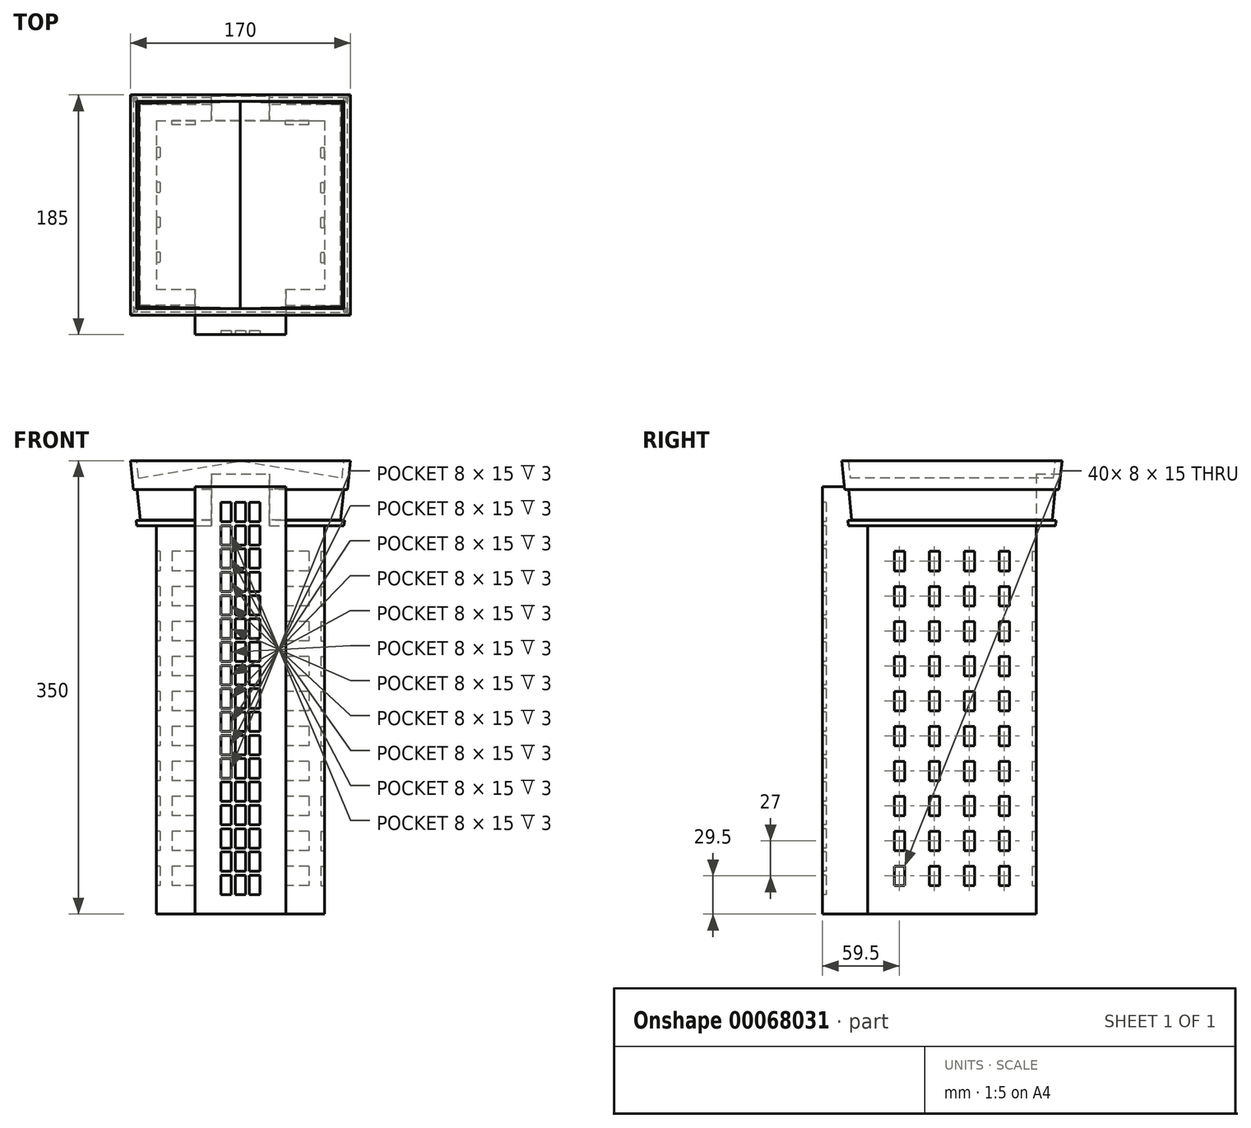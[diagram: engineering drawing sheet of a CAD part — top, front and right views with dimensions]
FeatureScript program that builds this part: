
annotation { "Feature Type Name" : "Feature", "Feature Type Description" : "" }
export const myFeature = defineFeature(function(context is Context, id is Id, definition is map)
    precondition{}
    {
        {
            var Q0;
            Q0=qCreatedBy(makeId("Top.planeOp"),FACE);
            var sketch = newSketch(context, id + "F0", { "sketchPlane" : qUnion([Q0])});
            skLineSegment(sketch, "E0.bottom", {"start": v(0, 0) * mm, "end": v(130, 0) * mm});
            skLineSegment(sketch, "E0.top", {"start": v(0, -130) * mm, "end": v(130, -130) * mm});
            skLineSegment(sketch, "E0.left", {"start": v(0, 0) * mm, "end": v(0, -130) * mm});
            skLineSegment(sketch, "E0.right", {"start": v(130, 0) * mm, "end": v(130, -130) * mm});
            skSolve(sketch);
        }
        {
            var Q0;
            Q0 = qSketchRegion(id + "F0", true);
            extrude(context, id + "F1", {"entities" : qUnion([Q0]), "depth" : 300 * mm});
        }
        {
            var Q0;
            Q0=makeQuery(id+"F1.opExtrude","SWEPT_FACE",FACE,{"disambiguationData":[OSD([sQuery(id+"F0.wireOp",EDGE,"E0.right")])]});
            var sketch = newSketch(context, id + "F2", { "sketchPlane" : qUnion([Q0])});
            skLineSegment(sketch, "E1.bottom", {"start": v(-109.5, 280) * mm, "end": v(-101.5, 280) * mm});
            skLineSegment(sketch, "E1.top", {"start": v(-109.5, 265) * mm, "end": v(-101.5, 265) * mm});
            skLineSegment(sketch, "E1.left", {"start": v(-109.5, 280) * mm, "end": v(-109.5, 265) * mm});
            skLineSegment(sketch, "E1.right", {"start": v(-101.5, 280) * mm, "end": v(-101.5, 265) * mm});
            skLineSegment(sketch, "E2.0.1.0", {"start": v(-109.5, 253) * mm, "end": v(-101.5, 253) * mm});
            skLineSegment(sketch, "E2.0.1.1", {"start": v(-109.5, 238) * mm, "end": v(-101.5, 238) * mm});
            skLineSegment(sketch, "E2.0.1.2", {"start": v(-109.5, 253) * mm, "end": v(-109.5, 238) * mm});
            skLineSegment(sketch, "E2.0.1.3", {"start": v(-101.5, 253) * mm, "end": v(-101.5, 238) * mm});
            skLineSegment(sketch, "E2.0.2.0", {"start": v(-109.5, 226) * mm, "end": v(-101.5, 226) * mm});
            skLineSegment(sketch, "E2.0.2.1", {"start": v(-109.5, 211) * mm, "end": v(-101.5, 211) * mm});
            skLineSegment(sketch, "E2.0.2.2", {"start": v(-109.5, 226) * mm, "end": v(-109.5, 211) * mm});
            skLineSegment(sketch, "E2.0.2.3", {"start": v(-101.5, 226) * mm, "end": v(-101.5, 211) * mm});
            skLineSegment(sketch, "E2.0.3.0", {"start": v(-109.5, 199) * mm, "end": v(-101.5, 199) * mm});
            skLineSegment(sketch, "E2.0.3.1", {"start": v(-109.5, 184) * mm, "end": v(-101.5, 184) * mm});
            skLineSegment(sketch, "E2.0.3.2", {"start": v(-109.5, 199) * mm, "end": v(-109.5, 184) * mm});
            skLineSegment(sketch, "E2.0.3.3", {"start": v(-101.5, 199) * mm, "end": v(-101.5, 184) * mm});
            skLineSegment(sketch, "E2.0.4.0", {"start": v(-109.5, 172) * mm, "end": v(-101.5, 172) * mm});
            skLineSegment(sketch, "E2.0.4.1", {"start": v(-109.5, 157) * mm, "end": v(-101.5, 157) * mm});
            skLineSegment(sketch, "E2.0.4.2", {"start": v(-109.5, 172) * mm, "end": v(-109.5, 157) * mm});
            skLineSegment(sketch, "E2.0.4.3", {"start": v(-101.5, 172) * mm, "end": v(-101.5, 157) * mm});
            skLineSegment(sketch, "E2.0.5.0", {"start": v(-109.5, 145) * mm, "end": v(-101.5, 145) * mm});
            skLineSegment(sketch, "E2.0.5.1", {"start": v(-109.5, 130) * mm, "end": v(-101.5, 130) * mm});
            skLineSegment(sketch, "E2.0.5.2", {"start": v(-109.5, 145) * mm, "end": v(-109.5, 130) * mm});
            skLineSegment(sketch, "E2.0.5.3", {"start": v(-101.5, 145) * mm, "end": v(-101.5, 130) * mm});
            skLineSegment(sketch, "E2.0.6.0", {"start": v(-109.5, 118) * mm, "end": v(-101.5, 118) * mm});
            skLineSegment(sketch, "E2.0.6.1", {"start": v(-109.5, 103) * mm, "end": v(-101.5, 103) * mm});
            skLineSegment(sketch, "E2.0.6.2", {"start": v(-109.5, 118) * mm, "end": v(-109.5, 103) * mm});
            skLineSegment(sketch, "E2.0.6.3", {"start": v(-101.5, 118) * mm, "end": v(-101.5, 103) * mm});
            skLineSegment(sketch, "E2.0.7.0", {"start": v(-109.5, 91) * mm, "end": v(-101.5, 91) * mm});
            skLineSegment(sketch, "E2.0.7.1", {"start": v(-109.5, 76) * mm, "end": v(-101.5, 76) * mm});
            skLineSegment(sketch, "E2.0.7.2", {"start": v(-109.5, 91) * mm, "end": v(-109.5, 76) * mm});
            skLineSegment(sketch, "E2.0.7.3", {"start": v(-101.5, 91) * mm, "end": v(-101.5, 76) * mm});
            skLineSegment(sketch, "E2.0.8.0", {"start": v(-109.5, 64) * mm, "end": v(-101.5, 64) * mm});
            skLineSegment(sketch, "E2.0.8.1", {"start": v(-109.5, 49) * mm, "end": v(-101.5, 49) * mm});
            skLineSegment(sketch, "E2.0.8.2", {"start": v(-109.5, 64) * mm, "end": v(-109.5, 49) * mm});
            skLineSegment(sketch, "E2.0.8.3", {"start": v(-101.5, 64) * mm, "end": v(-101.5, 49) * mm});
            skLineSegment(sketch, "E2.0.9.0", {"start": v(-109.5, 37) * mm, "end": v(-101.5, 37) * mm});
            skLineSegment(sketch, "E2.0.9.1", {"start": v(-109.5, 22) * mm, "end": v(-101.5, 22) * mm});
            skLineSegment(sketch, "E2.0.9.2", {"start": v(-109.5, 37) * mm, "end": v(-109.5, 22) * mm});
            skLineSegment(sketch, "E2.0.9.3", {"start": v(-101.5, 37) * mm, "end": v(-101.5, 22) * mm});
            skLineSegment(sketch, "E2.1.0.0", {"start": v(-82.5, 280) * mm, "end": v(-74.5, 280) * mm});
            skLineSegment(sketch, "E2.1.0.1", {"start": v(-82.5, 265) * mm, "end": v(-74.5, 265) * mm});
            skLineSegment(sketch, "E2.1.0.2", {"start": v(-82.5, 280) * mm, "end": v(-82.5, 265) * mm});
            skLineSegment(sketch, "E2.1.0.3", {"start": v(-74.5, 280) * mm, "end": v(-74.5, 265) * mm});
            skLineSegment(sketch, "E2.1.1.0", {"start": v(-82.5, 253) * mm, "end": v(-74.5, 253) * mm});
            skLineSegment(sketch, "E2.1.1.1", {"start": v(-82.5, 238) * mm, "end": v(-74.5, 238) * mm});
            skLineSegment(sketch, "E2.1.1.2", {"start": v(-82.5, 253) * mm, "end": v(-82.5, 238) * mm});
            skLineSegment(sketch, "E2.1.1.3", {"start": v(-74.5, 253) * mm, "end": v(-74.5, 238) * mm});
            skLineSegment(sketch, "E2.1.2.0", {"start": v(-82.5, 226) * mm, "end": v(-74.5, 226) * mm});
            skLineSegment(sketch, "E2.1.2.1", {"start": v(-82.5, 211) * mm, "end": v(-74.5, 211) * mm});
            skLineSegment(sketch, "E2.1.2.2", {"start": v(-82.5, 226) * mm, "end": v(-82.5, 211) * mm});
            skLineSegment(sketch, "E2.1.2.3", {"start": v(-74.5, 226) * mm, "end": v(-74.5, 211) * mm});
            skLineSegment(sketch, "E2.1.3.0", {"start": v(-82.5, 199) * mm, "end": v(-74.5, 199) * mm});
            skLineSegment(sketch, "E2.1.3.1", {"start": v(-82.5, 184) * mm, "end": v(-74.5, 184) * mm});
            skLineSegment(sketch, "E2.1.3.2", {"start": v(-82.5, 199) * mm, "end": v(-82.5, 184) * mm});
            skLineSegment(sketch, "E2.1.3.3", {"start": v(-74.5, 199) * mm, "end": v(-74.5, 184) * mm});
            skLineSegment(sketch, "E2.1.4.0", {"start": v(-82.5, 172) * mm, "end": v(-74.5, 172) * mm});
            skLineSegment(sketch, "E2.1.4.1", {"start": v(-82.5, 157) * mm, "end": v(-74.5, 157) * mm});
            skLineSegment(sketch, "E2.1.4.2", {"start": v(-82.5, 172) * mm, "end": v(-82.5, 157) * mm});
            skLineSegment(sketch, "E2.1.4.3", {"start": v(-74.5, 172) * mm, "end": v(-74.5, 157) * mm});
            skLineSegment(sketch, "E2.1.5.0", {"start": v(-82.5, 145) * mm, "end": v(-74.5, 145) * mm});
            skLineSegment(sketch, "E2.1.5.1", {"start": v(-82.5, 130) * mm, "end": v(-74.5, 130) * mm});
            skLineSegment(sketch, "E2.1.5.2", {"start": v(-82.5, 145) * mm, "end": v(-82.5, 130) * mm});
            skLineSegment(sketch, "E2.1.5.3", {"start": v(-74.5, 145) * mm, "end": v(-74.5, 130) * mm});
            skLineSegment(sketch, "E2.1.6.0", {"start": v(-82.5, 118) * mm, "end": v(-74.5, 118) * mm});
            skLineSegment(sketch, "E2.1.6.1", {"start": v(-82.5, 103) * mm, "end": v(-74.5, 103) * mm});
            skLineSegment(sketch, "E2.1.6.2", {"start": v(-82.5, 118) * mm, "end": v(-82.5, 103) * mm});
            skLineSegment(sketch, "E2.1.6.3", {"start": v(-74.5, 118) * mm, "end": v(-74.5, 103) * mm});
            skLineSegment(sketch, "E2.1.7.0", {"start": v(-82.5, 91) * mm, "end": v(-74.5, 91) * mm});
            skLineSegment(sketch, "E2.1.7.1", {"start": v(-82.5, 76) * mm, "end": v(-74.5, 76) * mm});
            skLineSegment(sketch, "E2.1.7.2", {"start": v(-82.5, 91) * mm, "end": v(-82.5, 76) * mm});
            skLineSegment(sketch, "E2.1.7.3", {"start": v(-74.5, 91) * mm, "end": v(-74.5, 76) * mm});
            skLineSegment(sketch, "E2.1.8.0", {"start": v(-82.5, 64) * mm, "end": v(-74.5, 64) * mm});
            skLineSegment(sketch, "E2.1.8.1", {"start": v(-82.5, 49) * mm, "end": v(-74.5, 49) * mm});
            skLineSegment(sketch, "E2.1.8.2", {"start": v(-82.5, 64) * mm, "end": v(-82.5, 49) * mm});
            skLineSegment(sketch, "E2.1.8.3", {"start": v(-74.5, 64) * mm, "end": v(-74.5, 49) * mm});
            skLineSegment(sketch, "E2.1.9.0", {"start": v(-82.5, 37) * mm, "end": v(-74.5, 37) * mm});
            skLineSegment(sketch, "E2.1.9.1", {"start": v(-82.5, 22) * mm, "end": v(-74.5, 22) * mm});
            skLineSegment(sketch, "E2.1.9.2", {"start": v(-82.5, 37) * mm, "end": v(-82.5, 22) * mm});
            skLineSegment(sketch, "E2.1.9.3", {"start": v(-74.5, 37) * mm, "end": v(-74.5, 22) * mm});
            skLineSegment(sketch, "E2.2.0.0", {"start": v(-55.5, 280) * mm, "end": v(-47.5, 280) * mm});
            skLineSegment(sketch, "E2.2.0.1", {"start": v(-55.5, 265) * mm, "end": v(-47.5, 265) * mm});
            skLineSegment(sketch, "E2.2.0.2", {"start": v(-55.5, 280) * mm, "end": v(-55.5, 265) * mm});
            skLineSegment(sketch, "E2.2.0.3", {"start": v(-47.5, 280) * mm, "end": v(-47.5, 265) * mm});
            skLineSegment(sketch, "E2.2.1.0", {"start": v(-55.5, 253) * mm, "end": v(-47.5, 253) * mm});
            skLineSegment(sketch, "E2.2.1.1", {"start": v(-55.5, 238) * mm, "end": v(-47.5, 238) * mm});
            skLineSegment(sketch, "E2.2.1.2", {"start": v(-55.5, 253) * mm, "end": v(-55.5, 238) * mm});
            skLineSegment(sketch, "E2.2.1.3", {"start": v(-47.5, 253) * mm, "end": v(-47.5, 238) * mm});
            skLineSegment(sketch, "E2.2.2.0", {"start": v(-55.5, 226) * mm, "end": v(-47.5, 226) * mm});
            skLineSegment(sketch, "E2.2.2.1", {"start": v(-55.5, 211) * mm, "end": v(-47.5, 211) * mm});
            skLineSegment(sketch, "E2.2.2.2", {"start": v(-55.5, 226) * mm, "end": v(-55.5, 211) * mm});
            skLineSegment(sketch, "E2.2.2.3", {"start": v(-47.5, 226) * mm, "end": v(-47.5, 211) * mm});
            skLineSegment(sketch, "E2.2.3.0", {"start": v(-55.5, 199) * mm, "end": v(-47.5, 199) * mm});
            skLineSegment(sketch, "E2.2.3.1", {"start": v(-55.5, 184) * mm, "end": v(-47.5, 184) * mm});
            skLineSegment(sketch, "E2.2.3.2", {"start": v(-55.5, 199) * mm, "end": v(-55.5, 184) * mm});
            skLineSegment(sketch, "E2.2.3.3", {"start": v(-47.5, 199) * mm, "end": v(-47.5, 184) * mm});
            skLineSegment(sketch, "E2.2.4.0", {"start": v(-55.5, 172) * mm, "end": v(-47.5, 172) * mm});
            skLineSegment(sketch, "E2.2.4.1", {"start": v(-55.5, 157) * mm, "end": v(-47.5, 157) * mm});
            skLineSegment(sketch, "E2.2.4.2", {"start": v(-55.5, 172) * mm, "end": v(-55.5, 157) * mm});
            skLineSegment(sketch, "E2.2.4.3", {"start": v(-47.5, 172) * mm, "end": v(-47.5, 157) * mm});
            skLineSegment(sketch, "E2.2.5.0", {"start": v(-55.5, 145) * mm, "end": v(-47.5, 145) * mm});
            skLineSegment(sketch, "E2.2.5.1", {"start": v(-55.5, 130) * mm, "end": v(-47.5, 130) * mm});
            skLineSegment(sketch, "E2.2.5.2", {"start": v(-55.5, 145) * mm, "end": v(-55.5, 130) * mm});
            skLineSegment(sketch, "E2.2.5.3", {"start": v(-47.5, 145) * mm, "end": v(-47.5, 130) * mm});
            skLineSegment(sketch, "E2.2.6.0", {"start": v(-55.5, 118) * mm, "end": v(-47.5, 118) * mm});
            skLineSegment(sketch, "E2.2.6.1", {"start": v(-55.5, 103) * mm, "end": v(-47.5, 103) * mm});
            skLineSegment(sketch, "E2.2.6.2", {"start": v(-55.5, 118) * mm, "end": v(-55.5, 103) * mm});
            skLineSegment(sketch, "E2.2.6.3", {"start": v(-47.5, 118) * mm, "end": v(-47.5, 103) * mm});
            skLineSegment(sketch, "E2.2.7.0", {"start": v(-55.5, 91) * mm, "end": v(-47.5, 91) * mm});
            skLineSegment(sketch, "E2.2.7.1", {"start": v(-55.5, 76) * mm, "end": v(-47.5, 76) * mm});
            skLineSegment(sketch, "E2.2.7.2", {"start": v(-55.5, 91) * mm, "end": v(-55.5, 76) * mm});
            skLineSegment(sketch, "E2.2.7.3", {"start": v(-47.5, 91) * mm, "end": v(-47.5, 76) * mm});
            skLineSegment(sketch, "E2.2.8.0", {"start": v(-55.5, 64) * mm, "end": v(-47.5, 64) * mm});
            skLineSegment(sketch, "E2.2.8.1", {"start": v(-55.5, 49) * mm, "end": v(-47.5, 49) * mm});
            skLineSegment(sketch, "E2.2.8.2", {"start": v(-55.5, 64) * mm, "end": v(-55.5, 49) * mm});
            skLineSegment(sketch, "E2.2.8.3", {"start": v(-47.5, 64) * mm, "end": v(-47.5, 49) * mm});
            skLineSegment(sketch, "E2.2.9.0", {"start": v(-55.5, 37) * mm, "end": v(-47.5, 37) * mm});
            skLineSegment(sketch, "E2.2.9.1", {"start": v(-55.5, 22) * mm, "end": v(-47.5, 22) * mm});
            skLineSegment(sketch, "E2.2.9.2", {"start": v(-55.5, 37) * mm, "end": v(-55.5, 22) * mm});
            skLineSegment(sketch, "E2.2.9.3", {"start": v(-47.5, 37) * mm, "end": v(-47.5, 22) * mm});
            skLineSegment(sketch, "E2.3.0.0", {"start": v(-28.5, 280) * mm, "end": v(-20.5, 280) * mm});
            skLineSegment(sketch, "E2.3.0.1", {"start": v(-28.5, 265) * mm, "end": v(-20.5, 265) * mm});
            skLineSegment(sketch, "E2.3.0.2", {"start": v(-28.5, 280) * mm, "end": v(-28.5, 265) * mm});
            skLineSegment(sketch, "E2.3.0.3", {"start": v(-20.5, 280) * mm, "end": v(-20.5, 265) * mm});
            skLineSegment(sketch, "E2.3.1.0", {"start": v(-28.5, 253) * mm, "end": v(-20.5, 253) * mm});
            skLineSegment(sketch, "E2.3.1.1", {"start": v(-28.5, 238) * mm, "end": v(-20.5, 238) * mm});
            skLineSegment(sketch, "E2.3.1.2", {"start": v(-28.5, 253) * mm, "end": v(-28.5, 238) * mm});
            skLineSegment(sketch, "E2.3.1.3", {"start": v(-20.5, 253) * mm, "end": v(-20.5, 238) * mm});
            skLineSegment(sketch, "E2.3.2.0", {"start": v(-28.5, 226) * mm, "end": v(-20.5, 226) * mm});
            skLineSegment(sketch, "E2.3.2.1", {"start": v(-28.5, 211) * mm, "end": v(-20.5, 211) * mm});
            skLineSegment(sketch, "E2.3.2.2", {"start": v(-28.5, 226) * mm, "end": v(-28.5, 211) * mm});
            skLineSegment(sketch, "E2.3.2.3", {"start": v(-20.5, 226) * mm, "end": v(-20.5, 211) * mm});
            skLineSegment(sketch, "E2.3.3.0", {"start": v(-28.5, 199) * mm, "end": v(-20.5, 199) * mm});
            skLineSegment(sketch, "E2.3.3.1", {"start": v(-28.5, 184) * mm, "end": v(-20.5, 184) * mm});
            skLineSegment(sketch, "E2.3.3.2", {"start": v(-28.5, 199) * mm, "end": v(-28.5, 184) * mm});
            skLineSegment(sketch, "E2.3.3.3", {"start": v(-20.5, 199) * mm, "end": v(-20.5, 184) * mm});
            skLineSegment(sketch, "E2.3.4.0", {"start": v(-28.5, 172) * mm, "end": v(-20.5, 172) * mm});
            skLineSegment(sketch, "E2.3.4.1", {"start": v(-28.5, 157) * mm, "end": v(-20.5, 157) * mm});
            skLineSegment(sketch, "E2.3.4.2", {"start": v(-28.5, 172) * mm, "end": v(-28.5, 157) * mm});
            skLineSegment(sketch, "E2.3.4.3", {"start": v(-20.5, 172) * mm, "end": v(-20.5, 157) * mm});
            skLineSegment(sketch, "E2.3.5.0", {"start": v(-28.5, 145) * mm, "end": v(-20.5, 145) * mm});
            skLineSegment(sketch, "E2.3.5.1", {"start": v(-28.5, 130) * mm, "end": v(-20.5, 130) * mm});
            skLineSegment(sketch, "E2.3.5.2", {"start": v(-28.5, 145) * mm, "end": v(-28.5, 130) * mm});
            skLineSegment(sketch, "E2.3.5.3", {"start": v(-20.5, 145) * mm, "end": v(-20.5, 130) * mm});
            skLineSegment(sketch, "E2.3.6.0", {"start": v(-28.5, 118) * mm, "end": v(-20.5, 118) * mm});
            skLineSegment(sketch, "E2.3.6.1", {"start": v(-28.5, 103) * mm, "end": v(-20.5, 103) * mm});
            skLineSegment(sketch, "E2.3.6.2", {"start": v(-28.5, 118) * mm, "end": v(-28.5, 103) * mm});
            skLineSegment(sketch, "E2.3.6.3", {"start": v(-20.5, 118) * mm, "end": v(-20.5, 103) * mm});
            skLineSegment(sketch, "E2.3.7.0", {"start": v(-28.5, 91) * mm, "end": v(-20.5, 91) * mm});
            skLineSegment(sketch, "E2.3.7.1", {"start": v(-28.5, 76) * mm, "end": v(-20.5, 76) * mm});
            skLineSegment(sketch, "E2.3.7.2", {"start": v(-28.5, 91) * mm, "end": v(-28.5, 76) * mm});
            skLineSegment(sketch, "E2.3.7.3", {"start": v(-20.5, 91) * mm, "end": v(-20.5, 76) * mm});
            skLineSegment(sketch, "E2.3.8.0", {"start": v(-28.5, 64) * mm, "end": v(-20.5, 64) * mm});
            skLineSegment(sketch, "E2.3.8.1", {"start": v(-28.5, 49) * mm, "end": v(-20.5, 49) * mm});
            skLineSegment(sketch, "E2.3.8.2", {"start": v(-28.5, 64) * mm, "end": v(-28.5, 49) * mm});
            skLineSegment(sketch, "E2.3.8.3", {"start": v(-20.5, 64) * mm, "end": v(-20.5, 49) * mm});
            skLineSegment(sketch, "E2.3.9.0", {"start": v(-28.5, 37) * mm, "end": v(-20.5, 37) * mm});
            skLineSegment(sketch, "E2.3.9.1", {"start": v(-28.5, 22) * mm, "end": v(-20.5, 22) * mm});
            skLineSegment(sketch, "E2.3.9.2", {"start": v(-28.5, 37) * mm, "end": v(-28.5, 22) * mm});
            skLineSegment(sketch, "E2.3.9.3", {"start": v(-20.5, 37) * mm, "end": v(-20.5, 22) * mm});
            skLineSegment(sketch, "E2.direction1", {"start": v(-109.5, 280) * mm, "end": v(-82.5, 280) * mm, "construction": true});
            skLineSegment(sketch, "E2.direction2", {"start": v(-109.5, 280) * mm, "end": v(-109.5, 253) * mm, "construction": true});
            skSolve(sketch);
        }
        {
            var Q0;
            Q0 = qSketchRegion(id + "F2", true);
            extrude(context, id + "F3", {"entities" : qUnion([Q0]), "operationType" : NewBodyOperationType.REMOVE, "oppositeDirection" : true, "depth" : 3 * mm});
        }
        {
            var Q0;
            Q0=makeQuery(id+"F1.opExtrude","SWEPT_FACE",FACE,{"disambiguationData":[OSD([sQuery(id+"F0.wireOp",EDGE,"E0.left")])]});
            var sketch = newSketch(context, id + "F4", { "sketchPlane" : qUnion([Q0])});
            skLineSegment(sketch, "E3.bottom", {"start": v(20.5, 280) * mm, "end": v(28.5, 280) * mm});
            skLineSegment(sketch, "E3.top", {"start": v(20.5, 265) * mm, "end": v(28.5, 265) * mm});
            skLineSegment(sketch, "E3.left", {"start": v(20.5, 280) * mm, "end": v(20.5, 265) * mm});
            skLineSegment(sketch, "E3.right", {"start": v(28.5, 280) * mm, "end": v(28.5, 265) * mm});
            skLineSegment(sketch, "E4.0.1.0", {"start": v(20.5, 253) * mm, "end": v(28.5, 253) * mm});
            skLineSegment(sketch, "E4.0.1.1", {"start": v(20.5, 238) * mm, "end": v(28.5, 238) * mm});
            skLineSegment(sketch, "E4.0.1.2", {"start": v(20.5, 253) * mm, "end": v(20.5, 238) * mm});
            skLineSegment(sketch, "E4.0.1.3", {"start": v(28.5, 253) * mm, "end": v(28.5, 238) * mm});
            skLineSegment(sketch, "E4.0.2.0", {"start": v(20.5, 226) * mm, "end": v(28.5, 226) * mm});
            skLineSegment(sketch, "E4.0.2.1", {"start": v(20.5, 211) * mm, "end": v(28.5, 211) * mm});
            skLineSegment(sketch, "E4.0.2.2", {"start": v(20.5, 226) * mm, "end": v(20.5, 211) * mm});
            skLineSegment(sketch, "E4.0.2.3", {"start": v(28.5, 226) * mm, "end": v(28.5, 211) * mm});
            skLineSegment(sketch, "E4.0.3.0", {"start": v(20.5, 199) * mm, "end": v(28.5, 199) * mm});
            skLineSegment(sketch, "E4.0.3.1", {"start": v(20.5, 184) * mm, "end": v(28.5, 184) * mm});
            skLineSegment(sketch, "E4.0.3.2", {"start": v(20.5, 199) * mm, "end": v(20.5, 184) * mm});
            skLineSegment(sketch, "E4.0.3.3", {"start": v(28.5, 199) * mm, "end": v(28.5, 184) * mm});
            skLineSegment(sketch, "E4.0.4.0", {"start": v(20.5, 172) * mm, "end": v(28.5, 172) * mm});
            skLineSegment(sketch, "E4.0.4.1", {"start": v(20.5, 157) * mm, "end": v(28.5, 157) * mm});
            skLineSegment(sketch, "E4.0.4.2", {"start": v(20.5, 172) * mm, "end": v(20.5, 157) * mm});
            skLineSegment(sketch, "E4.0.4.3", {"start": v(28.5, 172) * mm, "end": v(28.5, 157) * mm});
            skLineSegment(sketch, "E4.0.5.0", {"start": v(20.5, 145) * mm, "end": v(28.5, 145) * mm});
            skLineSegment(sketch, "E4.0.5.1", {"start": v(20.5, 130) * mm, "end": v(28.5, 130) * mm});
            skLineSegment(sketch, "E4.0.5.2", {"start": v(20.5, 145) * mm, "end": v(20.5, 130) * mm});
            skLineSegment(sketch, "E4.0.5.3", {"start": v(28.5, 145) * mm, "end": v(28.5, 130) * mm});
            skLineSegment(sketch, "E4.0.6.0", {"start": v(20.5, 118) * mm, "end": v(28.5, 118) * mm});
            skLineSegment(sketch, "E4.0.6.1", {"start": v(20.5, 103) * mm, "end": v(28.5, 103) * mm});
            skLineSegment(sketch, "E4.0.6.2", {"start": v(20.5, 118) * mm, "end": v(20.5, 103) * mm});
            skLineSegment(sketch, "E4.0.6.3", {"start": v(28.5, 118) * mm, "end": v(28.5, 103) * mm});
            skLineSegment(sketch, "E4.0.7.0", {"start": v(20.5, 91) * mm, "end": v(28.5, 91) * mm});
            skLineSegment(sketch, "E4.0.7.1", {"start": v(20.5, 76) * mm, "end": v(28.5, 76) * mm});
            skLineSegment(sketch, "E4.0.7.2", {"start": v(20.5, 91) * mm, "end": v(20.5, 76) * mm});
            skLineSegment(sketch, "E4.0.7.3", {"start": v(28.5, 91) * mm, "end": v(28.5, 76) * mm});
            skLineSegment(sketch, "E4.0.8.0", {"start": v(20.5, 64) * mm, "end": v(28.5, 64) * mm});
            skLineSegment(sketch, "E4.0.8.1", {"start": v(20.5, 49) * mm, "end": v(28.5, 49) * mm});
            skLineSegment(sketch, "E4.0.8.2", {"start": v(20.5, 64) * mm, "end": v(20.5, 49) * mm});
            skLineSegment(sketch, "E4.0.8.3", {"start": v(28.5, 64) * mm, "end": v(28.5, 49) * mm});
            skLineSegment(sketch, "E4.0.9.0", {"start": v(20.5, 37) * mm, "end": v(28.5, 37) * mm});
            skLineSegment(sketch, "E4.0.9.1", {"start": v(20.5, 22) * mm, "end": v(28.5, 22) * mm});
            skLineSegment(sketch, "E4.0.9.2", {"start": v(20.5, 37) * mm, "end": v(20.5, 22) * mm});
            skLineSegment(sketch, "E4.0.9.3", {"start": v(28.5, 37) * mm, "end": v(28.5, 22) * mm});
            skLineSegment(sketch, "E4.1.0.0", {"start": v(47.5, 280) * mm, "end": v(55.5, 280) * mm});
            skLineSegment(sketch, "E4.1.0.1", {"start": v(47.5, 265) * mm, "end": v(55.5, 265) * mm});
            skLineSegment(sketch, "E4.1.0.2", {"start": v(47.5, 280) * mm, "end": v(47.5, 265) * mm});
            skLineSegment(sketch, "E4.1.0.3", {"start": v(55.5, 280) * mm, "end": v(55.5, 265) * mm});
            skLineSegment(sketch, "E4.1.1.0", {"start": v(47.5, 253) * mm, "end": v(55.5, 253) * mm});
            skLineSegment(sketch, "E4.1.1.1", {"start": v(47.5, 238) * mm, "end": v(55.5, 238) * mm});
            skLineSegment(sketch, "E4.1.1.2", {"start": v(47.5, 253) * mm, "end": v(47.5, 238) * mm});
            skLineSegment(sketch, "E4.1.1.3", {"start": v(55.5, 253) * mm, "end": v(55.5, 238) * mm});
            skLineSegment(sketch, "E4.1.2.0", {"start": v(47.5, 226) * mm, "end": v(55.5, 226) * mm});
            skLineSegment(sketch, "E4.1.2.1", {"start": v(47.5, 211) * mm, "end": v(55.5, 211) * mm});
            skLineSegment(sketch, "E4.1.2.2", {"start": v(47.5, 226) * mm, "end": v(47.5, 211) * mm});
            skLineSegment(sketch, "E4.1.2.3", {"start": v(55.5, 226) * mm, "end": v(55.5, 211) * mm});
            skLineSegment(sketch, "E4.1.3.0", {"start": v(47.5, 199) * mm, "end": v(55.5, 199) * mm});
            skLineSegment(sketch, "E4.1.3.1", {"start": v(47.5, 184) * mm, "end": v(55.5, 184) * mm});
            skLineSegment(sketch, "E4.1.3.2", {"start": v(47.5, 199) * mm, "end": v(47.5, 184) * mm});
            skLineSegment(sketch, "E4.1.3.3", {"start": v(55.5, 199) * mm, "end": v(55.5, 184) * mm});
            skLineSegment(sketch, "E4.1.4.0", {"start": v(47.5, 172) * mm, "end": v(55.5, 172) * mm});
            skLineSegment(sketch, "E4.1.4.1", {"start": v(47.5, 157) * mm, "end": v(55.5, 157) * mm});
            skLineSegment(sketch, "E4.1.4.2", {"start": v(47.5, 172) * mm, "end": v(47.5, 157) * mm});
            skLineSegment(sketch, "E4.1.4.3", {"start": v(55.5, 172) * mm, "end": v(55.5, 157) * mm});
            skLineSegment(sketch, "E4.1.5.0", {"start": v(47.5, 145) * mm, "end": v(55.5, 145) * mm});
            skLineSegment(sketch, "E4.1.5.1", {"start": v(47.5, 130) * mm, "end": v(55.5, 130) * mm});
            skLineSegment(sketch, "E4.1.5.2", {"start": v(47.5, 145) * mm, "end": v(47.5, 130) * mm});
            skLineSegment(sketch, "E4.1.5.3", {"start": v(55.5, 145) * mm, "end": v(55.5, 130) * mm});
            skLineSegment(sketch, "E4.1.6.0", {"start": v(47.5, 118) * mm, "end": v(55.5, 118) * mm});
            skLineSegment(sketch, "E4.1.6.1", {"start": v(47.5, 103) * mm, "end": v(55.5, 103) * mm});
            skLineSegment(sketch, "E4.1.6.2", {"start": v(47.5, 118) * mm, "end": v(47.5, 103) * mm});
            skLineSegment(sketch, "E4.1.6.3", {"start": v(55.5, 118) * mm, "end": v(55.5, 103) * mm});
            skLineSegment(sketch, "E4.1.7.0", {"start": v(47.5, 91) * mm, "end": v(55.5, 91) * mm});
            skLineSegment(sketch, "E4.1.7.1", {"start": v(47.5, 76) * mm, "end": v(55.5, 76) * mm});
            skLineSegment(sketch, "E4.1.7.2", {"start": v(47.5, 91) * mm, "end": v(47.5, 76) * mm});
            skLineSegment(sketch, "E4.1.7.3", {"start": v(55.5, 91) * mm, "end": v(55.5, 76) * mm});
            skLineSegment(sketch, "E4.1.8.0", {"start": v(47.5, 64) * mm, "end": v(55.5, 64) * mm});
            skLineSegment(sketch, "E4.1.8.1", {"start": v(47.5, 49) * mm, "end": v(55.5, 49) * mm});
            skLineSegment(sketch, "E4.1.8.2", {"start": v(47.5, 64) * mm, "end": v(47.5, 49) * mm});
            skLineSegment(sketch, "E4.1.8.3", {"start": v(55.5, 64) * mm, "end": v(55.5, 49) * mm});
            skLineSegment(sketch, "E4.1.9.0", {"start": v(47.5, 37) * mm, "end": v(55.5, 37) * mm});
            skLineSegment(sketch, "E4.1.9.1", {"start": v(47.5, 22) * mm, "end": v(55.5, 22) * mm});
            skLineSegment(sketch, "E4.1.9.2", {"start": v(47.5, 37) * mm, "end": v(47.5, 22) * mm});
            skLineSegment(sketch, "E4.1.9.3", {"start": v(55.5, 37) * mm, "end": v(55.5, 22) * mm});
            skLineSegment(sketch, "E4.2.0.0", {"start": v(74.5, 280) * mm, "end": v(82.5, 280) * mm});
            skLineSegment(sketch, "E4.2.0.1", {"start": v(74.5, 265) * mm, "end": v(82.5, 265) * mm});
            skLineSegment(sketch, "E4.2.0.2", {"start": v(74.5, 280) * mm, "end": v(74.5, 265) * mm});
            skLineSegment(sketch, "E4.2.0.3", {"start": v(82.5, 280) * mm, "end": v(82.5, 265) * mm});
            skLineSegment(sketch, "E4.2.1.0", {"start": v(74.5, 253) * mm, "end": v(82.5, 253) * mm});
            skLineSegment(sketch, "E4.2.1.1", {"start": v(74.5, 238) * mm, "end": v(82.5, 238) * mm});
            skLineSegment(sketch, "E4.2.1.2", {"start": v(74.5, 253) * mm, "end": v(74.5, 238) * mm});
            skLineSegment(sketch, "E4.2.1.3", {"start": v(82.5, 253) * mm, "end": v(82.5, 238) * mm});
            skLineSegment(sketch, "E4.2.2.0", {"start": v(74.5, 226) * mm, "end": v(82.5, 226) * mm});
            skLineSegment(sketch, "E4.2.2.1", {"start": v(74.5, 211) * mm, "end": v(82.5, 211) * mm});
            skLineSegment(sketch, "E4.2.2.2", {"start": v(74.5, 226) * mm, "end": v(74.5, 211) * mm});
            skLineSegment(sketch, "E4.2.2.3", {"start": v(82.5, 226) * mm, "end": v(82.5, 211) * mm});
            skLineSegment(sketch, "E4.2.3.0", {"start": v(74.5, 199) * mm, "end": v(82.5, 199) * mm});
            skLineSegment(sketch, "E4.2.3.1", {"start": v(74.5, 184) * mm, "end": v(82.5, 184) * mm});
            skLineSegment(sketch, "E4.2.3.2", {"start": v(74.5, 199) * mm, "end": v(74.5, 184) * mm});
            skLineSegment(sketch, "E4.2.3.3", {"start": v(82.5, 199) * mm, "end": v(82.5, 184) * mm});
            skLineSegment(sketch, "E4.2.4.0", {"start": v(74.5, 172) * mm, "end": v(82.5, 172) * mm});
            skLineSegment(sketch, "E4.2.4.1", {"start": v(74.5, 157) * mm, "end": v(82.5, 157) * mm});
            skLineSegment(sketch, "E4.2.4.2", {"start": v(74.5, 172) * mm, "end": v(74.5, 157) * mm});
            skLineSegment(sketch, "E4.2.4.3", {"start": v(82.5, 172) * mm, "end": v(82.5, 157) * mm});
            skLineSegment(sketch, "E4.2.5.0", {"start": v(74.5, 145) * mm, "end": v(82.5, 145) * mm});
            skLineSegment(sketch, "E4.2.5.1", {"start": v(74.5, 130) * mm, "end": v(82.5, 130) * mm});
            skLineSegment(sketch, "E4.2.5.2", {"start": v(74.5, 145) * mm, "end": v(74.5, 130) * mm});
            skLineSegment(sketch, "E4.2.5.3", {"start": v(82.5, 145) * mm, "end": v(82.5, 130) * mm});
            skLineSegment(sketch, "E4.2.6.0", {"start": v(74.5, 118) * mm, "end": v(82.5, 118) * mm});
            skLineSegment(sketch, "E4.2.6.1", {"start": v(74.5, 103) * mm, "end": v(82.5, 103) * mm});
            skLineSegment(sketch, "E4.2.6.2", {"start": v(74.5, 118) * mm, "end": v(74.5, 103) * mm});
            skLineSegment(sketch, "E4.2.6.3", {"start": v(82.5, 118) * mm, "end": v(82.5, 103) * mm});
            skLineSegment(sketch, "E4.2.7.0", {"start": v(74.5, 91) * mm, "end": v(82.5, 91) * mm});
            skLineSegment(sketch, "E4.2.7.1", {"start": v(74.5, 76) * mm, "end": v(82.5, 76) * mm});
            skLineSegment(sketch, "E4.2.7.2", {"start": v(74.5, 91) * mm, "end": v(74.5, 76) * mm});
            skLineSegment(sketch, "E4.2.7.3", {"start": v(82.5, 91) * mm, "end": v(82.5, 76) * mm});
            skLineSegment(sketch, "E4.2.8.0", {"start": v(74.5, 64) * mm, "end": v(82.5, 64) * mm});
            skLineSegment(sketch, "E4.2.8.1", {"start": v(74.5, 49) * mm, "end": v(82.5, 49) * mm});
            skLineSegment(sketch, "E4.2.8.2", {"start": v(74.5, 64) * mm, "end": v(74.5, 49) * mm});
            skLineSegment(sketch, "E4.2.8.3", {"start": v(82.5, 64) * mm, "end": v(82.5, 49) * mm});
            skLineSegment(sketch, "E4.2.9.0", {"start": v(74.5, 37) * mm, "end": v(82.5, 37) * mm});
            skLineSegment(sketch, "E4.2.9.1", {"start": v(74.5, 22) * mm, "end": v(82.5, 22) * mm});
            skLineSegment(sketch, "E4.2.9.2", {"start": v(74.5, 37) * mm, "end": v(74.5, 22) * mm});
            skLineSegment(sketch, "E4.2.9.3", {"start": v(82.5, 37) * mm, "end": v(82.5, 22) * mm});
            skLineSegment(sketch, "E4.3.0.0", {"start": v(101.5, 280) * mm, "end": v(109.5, 280) * mm});
            skLineSegment(sketch, "E4.3.0.1", {"start": v(101.5, 265) * mm, "end": v(109.5, 265) * mm});
            skLineSegment(sketch, "E4.3.0.2", {"start": v(101.5, 280) * mm, "end": v(101.5, 265) * mm});
            skLineSegment(sketch, "E4.3.0.3", {"start": v(109.5, 280) * mm, "end": v(109.5, 265) * mm});
            skLineSegment(sketch, "E4.3.1.0", {"start": v(101.5, 253) * mm, "end": v(109.5, 253) * mm});
            skLineSegment(sketch, "E4.3.1.1", {"start": v(101.5, 238) * mm, "end": v(109.5, 238) * mm});
            skLineSegment(sketch, "E4.3.1.2", {"start": v(101.5, 253) * mm, "end": v(101.5, 238) * mm});
            skLineSegment(sketch, "E4.3.1.3", {"start": v(109.5, 253) * mm, "end": v(109.5, 238) * mm});
            skLineSegment(sketch, "E4.3.2.0", {"start": v(101.5, 226) * mm, "end": v(109.5, 226) * mm});
            skLineSegment(sketch, "E4.3.2.1", {"start": v(101.5, 211) * mm, "end": v(109.5, 211) * mm});
            skLineSegment(sketch, "E4.3.2.2", {"start": v(101.5, 226) * mm, "end": v(101.5, 211) * mm});
            skLineSegment(sketch, "E4.3.2.3", {"start": v(109.5, 226) * mm, "end": v(109.5, 211) * mm});
            skLineSegment(sketch, "E4.3.3.0", {"start": v(101.5, 199) * mm, "end": v(109.5, 199) * mm});
            skLineSegment(sketch, "E4.3.3.1", {"start": v(101.5, 184) * mm, "end": v(109.5, 184) * mm});
            skLineSegment(sketch, "E4.3.3.2", {"start": v(101.5, 199) * mm, "end": v(101.5, 184) * mm});
            skLineSegment(sketch, "E4.3.3.3", {"start": v(109.5, 199) * mm, "end": v(109.5, 184) * mm});
            skLineSegment(sketch, "E4.3.4.0", {"start": v(101.5, 172) * mm, "end": v(109.5, 172) * mm});
            skLineSegment(sketch, "E4.3.4.1", {"start": v(101.5, 157) * mm, "end": v(109.5, 157) * mm});
            skLineSegment(sketch, "E4.3.4.2", {"start": v(101.5, 172) * mm, "end": v(101.5, 157) * mm});
            skLineSegment(sketch, "E4.3.4.3", {"start": v(109.5, 172) * mm, "end": v(109.5, 157) * mm});
            skLineSegment(sketch, "E4.3.5.0", {"start": v(101.5, 145) * mm, "end": v(109.5, 145) * mm});
            skLineSegment(sketch, "E4.3.5.1", {"start": v(101.5, 130) * mm, "end": v(109.5, 130) * mm});
            skLineSegment(sketch, "E4.3.5.2", {"start": v(101.5, 145) * mm, "end": v(101.5, 130) * mm});
            skLineSegment(sketch, "E4.3.5.3", {"start": v(109.5, 145) * mm, "end": v(109.5, 130) * mm});
            skLineSegment(sketch, "E4.3.6.0", {"start": v(101.5, 118) * mm, "end": v(109.5, 118) * mm});
            skLineSegment(sketch, "E4.3.6.1", {"start": v(101.5, 103) * mm, "end": v(109.5, 103) * mm});
            skLineSegment(sketch, "E4.3.6.2", {"start": v(101.5, 118) * mm, "end": v(101.5, 103) * mm});
            skLineSegment(sketch, "E4.3.6.3", {"start": v(109.5, 118) * mm, "end": v(109.5, 103) * mm});
            skLineSegment(sketch, "E4.3.7.0", {"start": v(101.5, 91) * mm, "end": v(109.5, 91) * mm});
            skLineSegment(sketch, "E4.3.7.1", {"start": v(101.5, 76) * mm, "end": v(109.5, 76) * mm});
            skLineSegment(sketch, "E4.3.7.2", {"start": v(101.5, 91) * mm, "end": v(101.5, 76) * mm});
            skLineSegment(sketch, "E4.3.7.3", {"start": v(109.5, 91) * mm, "end": v(109.5, 76) * mm});
            skLineSegment(sketch, "E4.3.8.0", {"start": v(101.5, 64) * mm, "end": v(109.5, 64) * mm});
            skLineSegment(sketch, "E4.3.8.1", {"start": v(101.5, 49) * mm, "end": v(109.5, 49) * mm});
            skLineSegment(sketch, "E4.3.8.2", {"start": v(101.5, 64) * mm, "end": v(101.5, 49) * mm});
            skLineSegment(sketch, "E4.3.8.3", {"start": v(109.5, 64) * mm, "end": v(109.5, 49) * mm});
            skLineSegment(sketch, "E4.3.9.0", {"start": v(101.5, 37) * mm, "end": v(109.5, 37) * mm});
            skLineSegment(sketch, "E4.3.9.1", {"start": v(101.5, 22) * mm, "end": v(109.5, 22) * mm});
            skLineSegment(sketch, "E4.3.9.2", {"start": v(101.5, 37) * mm, "end": v(101.5, 22) * mm});
            skLineSegment(sketch, "E4.3.9.3", {"start": v(109.5, 37) * mm, "end": v(109.5, 22) * mm});
            skLineSegment(sketch, "E4.direction1", {"start": v(20.5, 280) * mm, "end": v(47.5, 280) * mm, "construction": true});
            skLineSegment(sketch, "E4.direction2", {"start": v(20.5, 280) * mm, "end": v(20.5, 253) * mm, "construction": true});
            skSolve(sketch);
        }
        {
            var Q0;
            Q0 = qSketchRegion(id + "F4", true);
            extrude(context, id + "F5", {"entities" : qUnion([Q0]), "operationType" : NewBodyOperationType.REMOVE, "oppositeDirection" : true, "depth" : 3 * mm});
        }
        {
            var Q0;
            Q0=makeQuery(id+"F1.opExtrude","SWEPT_FACE",FACE,{"disambiguationData":[OSD([sQuery(id+"F0.wireOp",EDGE,"E0.bottom")])]});
            var sketch = newSketch(context, id + "F6", { "sketchPlane" : qUnion([Q0])});
            skLineSegment(sketch, "E5.bottom", {"start": v(-117.75, 280) * mm, "end": v(-99.75, 280) * mm});
            skLineSegment(sketch, "E5.top", {"start": v(-117.75, 265) * mm, "end": v(-99.75, 265) * mm});
            skLineSegment(sketch, "E5.left", {"start": v(-117.75, 280) * mm, "end": v(-117.75, 265) * mm});
            skLineSegment(sketch, "E5.right", {"start": v(-99.75, 280) * mm, "end": v(-99.75, 265) * mm});
            skLineSegment(sketch, "E6.0.1.0", {"start": v(-117.75, 253) * mm, "end": v(-99.75, 253) * mm});
            skLineSegment(sketch, "E6.0.1.1", {"start": v(-117.75, 238) * mm, "end": v(-99.75, 238) * mm});
            skLineSegment(sketch, "E6.0.1.2", {"start": v(-117.75, 253) * mm, "end": v(-117.75, 238) * mm});
            skLineSegment(sketch, "E6.0.1.3", {"start": v(-99.75, 253) * mm, "end": v(-99.75, 238) * mm});
            skLineSegment(sketch, "E6.0.2.0", {"start": v(-117.75, 226) * mm, "end": v(-99.75, 226) * mm});
            skLineSegment(sketch, "E6.0.2.1", {"start": v(-117.75, 211) * mm, "end": v(-99.75, 211) * mm});
            skLineSegment(sketch, "E6.0.2.2", {"start": v(-117.75, 226) * mm, "end": v(-117.75, 211) * mm});
            skLineSegment(sketch, "E6.0.2.3", {"start": v(-99.75, 226) * mm, "end": v(-99.75, 211) * mm});
            skLineSegment(sketch, "E6.0.3.0", {"start": v(-117.75, 199) * mm, "end": v(-99.75, 199) * mm});
            skLineSegment(sketch, "E6.0.3.1", {"start": v(-117.75, 184) * mm, "end": v(-99.75, 184) * mm});
            skLineSegment(sketch, "E6.0.3.2", {"start": v(-117.75, 199) * mm, "end": v(-117.75, 184) * mm});
            skLineSegment(sketch, "E6.0.3.3", {"start": v(-99.75, 199) * mm, "end": v(-99.75, 184) * mm});
            skLineSegment(sketch, "E6.0.4.0", {"start": v(-117.75, 172) * mm, "end": v(-99.75, 172) * mm});
            skLineSegment(sketch, "E6.0.4.1", {"start": v(-117.75, 157) * mm, "end": v(-99.75, 157) * mm});
            skLineSegment(sketch, "E6.0.4.2", {"start": v(-117.75, 172) * mm, "end": v(-117.75, 157) * mm});
            skLineSegment(sketch, "E6.0.4.3", {"start": v(-99.75, 172) * mm, "end": v(-99.75, 157) * mm});
            skLineSegment(sketch, "E6.0.5.0", {"start": v(-117.75, 145) * mm, "end": v(-99.75, 145) * mm});
            skLineSegment(sketch, "E6.0.5.1", {"start": v(-117.75, 130) * mm, "end": v(-99.75, 130) * mm});
            skLineSegment(sketch, "E6.0.5.2", {"start": v(-117.75, 145) * mm, "end": v(-117.75, 130) * mm});
            skLineSegment(sketch, "E6.0.5.3", {"start": v(-99.75, 145) * mm, "end": v(-99.75, 130) * mm});
            skLineSegment(sketch, "E6.0.6.0", {"start": v(-117.75, 118) * mm, "end": v(-99.75, 118) * mm});
            skLineSegment(sketch, "E6.0.6.1", {"start": v(-117.75, 103) * mm, "end": v(-99.75, 103) * mm});
            skLineSegment(sketch, "E6.0.6.2", {"start": v(-117.75, 118) * mm, "end": v(-117.75, 103) * mm});
            skLineSegment(sketch, "E6.0.6.3", {"start": v(-99.75, 118) * mm, "end": v(-99.75, 103) * mm});
            skLineSegment(sketch, "E6.0.7.0", {"start": v(-117.75, 91) * mm, "end": v(-99.75, 91) * mm});
            skLineSegment(sketch, "E6.0.7.1", {"start": v(-117.75, 76) * mm, "end": v(-99.75, 76) * mm});
            skLineSegment(sketch, "E6.0.7.2", {"start": v(-117.75, 91) * mm, "end": v(-117.75, 76) * mm});
            skLineSegment(sketch, "E6.0.7.3", {"start": v(-99.75, 91) * mm, "end": v(-99.75, 76) * mm});
            skLineSegment(sketch, "E6.0.8.0", {"start": v(-117.75, 64) * mm, "end": v(-99.75, 64) * mm});
            skLineSegment(sketch, "E6.0.8.1", {"start": v(-117.75, 49) * mm, "end": v(-99.75, 49) * mm});
            skLineSegment(sketch, "E6.0.8.2", {"start": v(-117.75, 64) * mm, "end": v(-117.75, 49) * mm});
            skLineSegment(sketch, "E6.0.8.3", {"start": v(-99.75, 64) * mm, "end": v(-99.75, 49) * mm});
            skLineSegment(sketch, "E6.0.9.0", {"start": v(-117.75, 37) * mm, "end": v(-99.75, 37) * mm});
            skLineSegment(sketch, "E6.0.9.1", {"start": v(-117.75, 22) * mm, "end": v(-99.75, 22) * mm});
            skLineSegment(sketch, "E6.0.9.2", {"start": v(-117.75, 37) * mm, "end": v(-117.75, 22) * mm});
            skLineSegment(sketch, "E6.0.9.3", {"start": v(-99.75, 37) * mm, "end": v(-99.75, 22) * mm});
            skLineSegment(sketch, "E6.1.0.0", {"start": v(-30.25, 280) * mm, "end": v(-12.25, 280) * mm});
            skLineSegment(sketch, "E6.1.0.1", {"start": v(-30.25, 265) * mm, "end": v(-12.25, 265) * mm});
            skLineSegment(sketch, "E6.1.0.2", {"start": v(-30.25, 280) * mm, "end": v(-30.25, 265) * mm});
            skLineSegment(sketch, "E6.1.0.3", {"start": v(-12.25, 280) * mm, "end": v(-12.25, 265) * mm});
            skLineSegment(sketch, "E6.1.1.0", {"start": v(-30.25, 253) * mm, "end": v(-12.25, 253) * mm});
            skLineSegment(sketch, "E6.1.1.1", {"start": v(-30.25, 238) * mm, "end": v(-12.25, 238) * mm});
            skLineSegment(sketch, "E6.1.1.2", {"start": v(-30.25, 253) * mm, "end": v(-30.25, 238) * mm});
            skLineSegment(sketch, "E6.1.1.3", {"start": v(-12.25, 253) * mm, "end": v(-12.25, 238) * mm});
            skLineSegment(sketch, "E6.1.2.0", {"start": v(-30.25, 226) * mm, "end": v(-12.25, 226) * mm});
            skLineSegment(sketch, "E6.1.2.1", {"start": v(-30.25, 211) * mm, "end": v(-12.25, 211) * mm});
            skLineSegment(sketch, "E6.1.2.2", {"start": v(-30.25, 226) * mm, "end": v(-30.25, 211) * mm});
            skLineSegment(sketch, "E6.1.2.3", {"start": v(-12.25, 226) * mm, "end": v(-12.25, 211) * mm});
            skLineSegment(sketch, "E6.1.3.0", {"start": v(-30.25, 199) * mm, "end": v(-12.25, 199) * mm});
            skLineSegment(sketch, "E6.1.3.1", {"start": v(-30.25, 184) * mm, "end": v(-12.25, 184) * mm});
            skLineSegment(sketch, "E6.1.3.2", {"start": v(-30.25, 199) * mm, "end": v(-30.25, 184) * mm});
            skLineSegment(sketch, "E6.1.3.3", {"start": v(-12.25, 199) * mm, "end": v(-12.25, 184) * mm});
            skLineSegment(sketch, "E6.1.4.0", {"start": v(-30.25, 172) * mm, "end": v(-12.25, 172) * mm});
            skLineSegment(sketch, "E6.1.4.1", {"start": v(-30.25, 157) * mm, "end": v(-12.25, 157) * mm});
            skLineSegment(sketch, "E6.1.4.2", {"start": v(-30.25, 172) * mm, "end": v(-30.25, 157) * mm});
            skLineSegment(sketch, "E6.1.4.3", {"start": v(-12.25, 172) * mm, "end": v(-12.25, 157) * mm});
            skLineSegment(sketch, "E6.1.5.0", {"start": v(-30.25, 145) * mm, "end": v(-12.25, 145) * mm});
            skLineSegment(sketch, "E6.1.5.1", {"start": v(-30.25, 130) * mm, "end": v(-12.25, 130) * mm});
            skLineSegment(sketch, "E6.1.5.2", {"start": v(-30.25, 145) * mm, "end": v(-30.25, 130) * mm});
            skLineSegment(sketch, "E6.1.5.3", {"start": v(-12.25, 145) * mm, "end": v(-12.25, 130) * mm});
            skLineSegment(sketch, "E6.1.6.0", {"start": v(-30.25, 118) * mm, "end": v(-12.25, 118) * mm});
            skLineSegment(sketch, "E6.1.6.1", {"start": v(-30.25, 103) * mm, "end": v(-12.25, 103) * mm});
            skLineSegment(sketch, "E6.1.6.2", {"start": v(-30.25, 118) * mm, "end": v(-30.25, 103) * mm});
            skLineSegment(sketch, "E6.1.6.3", {"start": v(-12.25, 118) * mm, "end": v(-12.25, 103) * mm});
            skLineSegment(sketch, "E6.1.7.0", {"start": v(-30.25, 91) * mm, "end": v(-12.25, 91) * mm});
            skLineSegment(sketch, "E6.1.7.1", {"start": v(-30.25, 76) * mm, "end": v(-12.25, 76) * mm});
            skLineSegment(sketch, "E6.1.7.2", {"start": v(-30.25, 91) * mm, "end": v(-30.25, 76) * mm});
            skLineSegment(sketch, "E6.1.7.3", {"start": v(-12.25, 91) * mm, "end": v(-12.25, 76) * mm});
            skLineSegment(sketch, "E6.1.8.0", {"start": v(-30.25, 64) * mm, "end": v(-12.25, 64) * mm});
            skLineSegment(sketch, "E6.1.8.1", {"start": v(-30.25, 49) * mm, "end": v(-12.25, 49) * mm});
            skLineSegment(sketch, "E6.1.8.2", {"start": v(-30.25, 64) * mm, "end": v(-30.25, 49) * mm});
            skLineSegment(sketch, "E6.1.8.3", {"start": v(-12.25, 64) * mm, "end": v(-12.25, 49) * mm});
            skLineSegment(sketch, "E6.1.9.0", {"start": v(-30.25, 37) * mm, "end": v(-12.25, 37) * mm});
            skLineSegment(sketch, "E6.1.9.1", {"start": v(-30.25, 22) * mm, "end": v(-12.25, 22) * mm});
            skLineSegment(sketch, "E6.1.9.2", {"start": v(-30.25, 37) * mm, "end": v(-30.25, 22) * mm});
            skLineSegment(sketch, "E6.1.9.3", {"start": v(-12.25, 37) * mm, "end": v(-12.25, 22) * mm});
            skLineSegment(sketch, "E6.direction1", {"start": v(-117.75, 280) * mm, "end": v(-30.25, 280) * mm, "construction": true});
            skLineSegment(sketch, "E6.direction2", {"start": v(-117.75, 280) * mm, "end": v(-117.75, 253) * mm, "construction": true});
            skSolve(sketch);
        }
        {
            var Q0;
            Q0 = qSketchRegion(id + "F6", true);
            extrude(context, id + "F7", {"entities" : qUnion([Q0]), "operationType" : NewBodyOperationType.REMOVE, "oppositeDirection" : true, "depth" : 3 * mm});
        }
        {
            var Q0;
            Q0=makeQuery(id+"F1.opExtrude","CAP_FACE",FACE,{"disambiguationData":[OSD([sQuery(id+"F0.wireOp",EDGE,"E0.bottom"),sQuery(id+"F0.wireOp",EDGE,"E0.top"),sQuery(id+"F0.wireOp",EDGE,"E0.left"),sQuery(id+"F0.wireOp",EDGE,"E0.right")])],"isStart":false});
            var sketch = newSketch(context, id + "F8", { "sketchPlane" : qUnion([Q0])});
            skLineSegment(sketch, "E7.bottom", {"start": v(-15, 15) * mm, "end": v(145, 15) * mm});
            skLineSegment(sketch, "E7.top", {"start": v(-15, -145) * mm, "end": v(145, -145) * mm});
            skLineSegment(sketch, "E7.left", {"start": v(-15, 15) * mm, "end": v(-15, -145) * mm});
            skLineSegment(sketch, "E7.right", {"start": v(145, 15) * mm, "end": v(145, -145) * mm});
            skSolve(sketch);
        }
        {
            var Q0;
            Q0=makeQuery(id+"F8.imprint","IMPRINT",FACE,{"disambiguationData":[TD([[makeQuery(id+"F8.imprint","IMPRINT",EDGE,{"derivedFrom":makeQuery(id+"F1.opExtrude","CAP_EDGE",EDGE,{"disambiguationData":[OSD([sQuery(id+"F0.wireOp",EDGE,"E0.bottom")])],"isStart":false})}),-1.0]])]});
            cPlane(context, id + "F9", {"entities" : qUnion([Q0]), "cplaneType" : CPlaneType.OFFSET, "offset" : 50 * mm, "width" : 150 * mm, "height" : 150 * mm});
        }
        {
            var Q0;
            Q0=qCreatedBy(id+"F9.planeOp",FACE);
            var sketch = newSketch(context, id + "F10", { "sketchPlane" : qUnion([Q0])});
            skLineSegment(sketch, "E8.bottom", {"start": v(-20, 20) * mm, "end": v(150, 20) * mm});
            skLineSegment(sketch, "E8.top", {"start": v(-20, -150) * mm, "end": v(150, -150) * mm});
            skLineSegment(sketch, "E8.left", {"start": v(-20, 20) * mm, "end": v(-20, -150) * mm});
            skLineSegment(sketch, "E8.right", {"start": v(150, 20) * mm, "end": v(150, -150) * mm});
            skSolve(sketch);
        }
        {
            var Q0;
            Q0 = qSketchRegion(id + "F10", true);
            var Q1;
            Q1 = qSketchRegion(id + "F8", true);
            loft(context, id + "F11", {"operationType" : NewBodyOperationType.ADD, "sheetProfilesArray" : [{ "sheetProfileEntities" : qUnion([Q0]) }, { "sheetProfileEntities" : qUnion([Q1]) }]});
        }
        {
            var Q0;
            Q0=makeQuery(id+"F11.opLoft","CAP_FACE",FACE,{"disambiguationData":[OSD([makeQuery(id+"F10.imprint","IMPRINT",FACE,{"disambiguationData":[TD([[makeQuery(id+"F10.imprint","IMPRINT",EDGE,{"derivedFrom":sQuery(id+"F10.wireOp",EDGE,"E8.bottom")}),-1.0]])]})])],"isStart":true});
            var sketch = newSketch(context, id + "F12", { "sketchPlane" : qUnion([Q0])});
            skLineSegment(sketch, "E9.bottom", {"start": v(-15, -145) * mm, "end": v(145, -145) * mm});
            skLineSegment(sketch, "E9.top", {"start": v(-15, 15) * mm, "end": v(145, 15) * mm});
            skLineSegment(sketch, "E9.left", {"start": v(-15, -145) * mm, "end": v(-15, 15) * mm});
            skLineSegment(sketch, "E9.right", {"start": v(145, -145) * mm, "end": v(145, 15) * mm});
            skSolve(sketch);
        }
        {
            var Q0;
            Q0=makeQuery(id+"F12.imprint","IMPRINT",FACE,{"disambiguationData":[TD([[makeQuery(id+"F12.imprint","IMPRINT",EDGE,{"derivedFrom":sQuery(id+"F12.wireOp",EDGE,"E9.bottom")}),1.0]])]});
            cPlane(context, id + "F13", {"entities" : qUnion([Q0]), "cplaneType" : CPlaneType.OFFSET, "offset" : 45 * mm, "oppositeDirection" : true, "width" : 150 * mm, "height" : 150 * mm});
        }
        {
            var Q0;
            Q0=qCreatedBy(id+"F13.planeOp",FACE);
            var sketch = newSketch(context, id + "F14", { "sketchPlane" : qUnion([Q0])});
            skLineSegment(sketch, "E10.bottom", {"start": v(-10, -140) * mm, "end": v(140, -140) * mm});
            skLineSegment(sketch, "E10.top", {"start": v(-10, 10) * mm, "end": v(140, 10) * mm});
            skLineSegment(sketch, "E10.left", {"start": v(-10, -140) * mm, "end": v(-10, 10) * mm});
            skLineSegment(sketch, "E10.right", {"start": v(140, -140) * mm, "end": v(140, 10) * mm});
            skSolve(sketch);
        }
        {
            var Q0;
            Q0 = qSketchRegion(id + "F14", true);
            var Q1;
            Q1 = qSketchRegion(id + "F12", true);
            loft(context, id + "F15", {"operationType" : NewBodyOperationType.REMOVE, "sheetProfilesArray" : [{ "sheetProfileEntities" : qUnion([Q0]) }, { "sheetProfileEntities" : qUnion([Q1]) }]});
        }
        {
            var Q0;
            Q0=qCreatedBy(makeId("Front.planeOp"),FACE);
            cPlane(context, id + "F16", {"entities" : qUnion([Q0]), "cplaneType" : CPlaneType.OFFSET, "offset" : 65 * mm, "width" : 150 * mm, "height" : 150 * mm});
        }
        {
            var Q0;
            Q0=qCreatedBy(id+"F16.planeOp",FACE);
            var sketch = newSketch(context, id + "F17", { "sketchPlane" : qUnion([Q0])});
            skLineSegment(sketch, "E11", {"start": v(-15, 300) * mm, "end": v(-18.59, 335.9) * mm});
            skLineSegment(sketch, "E12", {"start": v(148.59, 335.9) * mm, "end": v(145, 300) * mm});
            skLineSegment(sketch, "E13", {"start": v(145, 300) * mm, "end": v(-15, 300) * mm});
            skLineSegment(sketch, "E14", {"start": v(-18.59, 335.9) * mm, "end": v(65, 350) * mm});
            skLineSegment(sketch, "E15", {"start": v(65, 350) * mm, "end": v(148.59, 335.9) * mm});
            skSolve(sketch);
        }
        {
            var Q0;
            Q0 = qSketchRegion(id + "F17", true);
            var Q1;
            Q1=makeQuery(id+"F15.boolean.opBoolean","COPY",FACE,{"derivedFrom":makeQuery(id+"F15.opLoft","SWEPT_FACE",FACE,{"disambiguationData":[OSD([sQuery(id+"F12.wireOp",EDGE,"E9.bottom"),sQuery(id+"F12.wireOp",EDGE,"E9.left"),sQuery(id+"F12.wireOp",EDGE,"E9.right"),sQuery(id+"F14.wireOp",EDGE,"E10.bottom"),sQuery(id+"F14.wireOp",EDGE,"E10.left"),sQuery(id+"F14.wireOp",EDGE,"E10.right")])]})});
            var Q2;
            Q2=makeQuery(id+"F15.boolean.opBoolean","COPY",FACE,{"derivedFrom":makeQuery(id+"F15.opLoft","SWEPT_FACE",FACE,{"disambiguationData":[OSD([sQuery(id+"F12.wireOp",EDGE,"E9.top"),sQuery(id+"F12.wireOp",EDGE,"E9.left"),sQuery(id+"F12.wireOp",EDGE,"E9.right"),sQuery(id+"F14.wireOp",EDGE,"E10.top"),sQuery(id+"F14.wireOp",EDGE,"E10.left"),sQuery(id+"F14.wireOp",EDGE,"E10.right")])]})});
            extrude(context, id + "F18", {"entities" : qUnion([Q0]), "operationType" : NewBodyOperationType.ADD, "endBound" : BoundingType.UP_TO_SURFACE, "endBoundEntityFace" : qUnion([Q1]), "depth" : 25 * mm, "hasSecondDirection" : true, "secondDirectionBound" : SecondDirectionBoundingType.UP_TO_SURFACE, "secondDirectionOppositeDirection" : true, "secondDirectionBoundEntityFace" : qUnion([Q2]), "secondDirectionDepth" : 25 * mm});
        }
        {
            var Q0;
            Q0=makeQuery(id+"F1.opExtrude","CAP_FACE",FACE,{"disambiguationData":[OSD([sQuery(id+"F0.wireOp",EDGE,"E0.bottom"),sQuery(id+"F0.wireOp",EDGE,"E0.top"),sQuery(id+"F0.wireOp",EDGE,"E0.left"),sQuery(id+"F0.wireOp",EDGE,"E0.right")])],"isStart":true});
            var sketch = newSketch(context, id + "F19", { "sketchPlane" : qUnion([Q0])});
            skLineSegment(sketch, "E16.bottom", {"start": v(30, 130) * mm, "end": v(100, 130) * mm});
            skLineSegment(sketch, "E16.top", {"start": v(30, 165) * mm, "end": v(100, 165) * mm});
            skLineSegment(sketch, "E16.left", {"start": v(30, 130) * mm, "end": v(30, 165) * mm});
            skLineSegment(sketch, "E16.right", {"start": v(100, 130) * mm, "end": v(100, 165) * mm});
            skSolve(sketch);
        }
        {
            var Q0;
            Q0=makeQuery(id+"F19.imprint","IMPRINT",FACE,{"disambiguationData":[TD([[makeQuery(id+"F19.imprint","IMPRINT",EDGE,{"derivedFrom":sQuery(id+"F19.wireOp",EDGE,"E16.bottom")}),1.0]])]});
            extrude(context, id + "F20", {"entities" : qUnion([Q0]), "operationType" : NewBodyOperationType.ADD, "oppositeDirection" : true, "depth" : 330 * mm});
        }
        {
            var Q0;
            Q0=makeQuery(id+"F20.opExtrude","SWEPT_FACE",FACE,{"disambiguationData":[OSD([sQuery(id+"F19.wireOp",EDGE,"E16.top")])]});
            var sketch = newSketch(context, id + "F21", { "sketchPlane" : qUnion([Q0])});
            skLineSegment(sketch, "E17.bottom", {"start": v(50, 318) * mm, "end": v(58, 318) * mm});
            skLineSegment(sketch, "E17.top", {"start": v(50, 303) * mm, "end": v(58, 303) * mm});
            skLineSegment(sketch, "E17.left", {"start": v(50, 318) * mm, "end": v(50, 303) * mm});
            skLineSegment(sketch, "E17.right", {"start": v(58, 318) * mm, "end": v(58, 303) * mm});
            skLineSegment(sketch, "E18.0.1.0", {"start": v(50, 300) * mm, "end": v(58, 300) * mm});
            skLineSegment(sketch, "E18.0.1.1", {"start": v(50, 285) * mm, "end": v(58, 285) * mm});
            skLineSegment(sketch, "E18.0.1.2", {"start": v(50, 300) * mm, "end": v(50, 285) * mm});
            skLineSegment(sketch, "E18.0.1.3", {"start": v(58, 300) * mm, "end": v(58, 285) * mm});
            skLineSegment(sketch, "E18.0.2.0", {"start": v(50, 282) * mm, "end": v(58, 282) * mm});
            skLineSegment(sketch, "E18.0.2.1", {"start": v(50, 267) * mm, "end": v(58, 267) * mm});
            skLineSegment(sketch, "E18.0.2.2", {"start": v(50, 282) * mm, "end": v(50, 267) * mm});
            skLineSegment(sketch, "E18.0.2.3", {"start": v(58, 282) * mm, "end": v(58, 267) * mm});
            skLineSegment(sketch, "E18.0.3.0", {"start": v(50, 264) * mm, "end": v(58, 264) * mm});
            skLineSegment(sketch, "E18.0.3.1", {"start": v(50, 249) * mm, "end": v(58, 249) * mm});
            skLineSegment(sketch, "E18.0.3.2", {"start": v(50, 264) * mm, "end": v(50, 249) * mm});
            skLineSegment(sketch, "E18.0.3.3", {"start": v(58, 264) * mm, "end": v(58, 249) * mm});
            skLineSegment(sketch, "E18.0.4.0", {"start": v(50, 246) * mm, "end": v(58, 246) * mm});
            skLineSegment(sketch, "E18.0.4.1", {"start": v(50, 231) * mm, "end": v(58, 231) * mm});
            skLineSegment(sketch, "E18.0.4.2", {"start": v(50, 246) * mm, "end": v(50, 231) * mm});
            skLineSegment(sketch, "E18.0.4.3", {"start": v(58, 246) * mm, "end": v(58, 231) * mm});
            skLineSegment(sketch, "E18.0.5.0", {"start": v(50, 228) * mm, "end": v(58, 228) * mm});
            skLineSegment(sketch, "E18.0.5.1", {"start": v(50, 213) * mm, "end": v(58, 213) * mm});
            skLineSegment(sketch, "E18.0.5.2", {"start": v(50, 228) * mm, "end": v(50, 213) * mm});
            skLineSegment(sketch, "E18.0.5.3", {"start": v(58, 228) * mm, "end": v(58, 213) * mm});
            skLineSegment(sketch, "E18.0.6.0", {"start": v(50, 210) * mm, "end": v(58, 210) * mm});
            skLineSegment(sketch, "E18.0.6.1", {"start": v(50, 195) * mm, "end": v(58, 195) * mm});
            skLineSegment(sketch, "E18.0.6.2", {"start": v(50, 210) * mm, "end": v(50, 195) * mm});
            skLineSegment(sketch, "E18.0.6.3", {"start": v(58, 210) * mm, "end": v(58, 195) * mm});
            skLineSegment(sketch, "E18.0.7.0", {"start": v(50, 192) * mm, "end": v(58, 192) * mm});
            skLineSegment(sketch, "E18.0.7.1", {"start": v(50, 177) * mm, "end": v(58, 177) * mm});
            skLineSegment(sketch, "E18.0.7.2", {"start": v(50, 192) * mm, "end": v(50, 177) * mm});
            skLineSegment(sketch, "E18.0.7.3", {"start": v(58, 192) * mm, "end": v(58, 177) * mm});
            skLineSegment(sketch, "E18.0.8.0", {"start": v(50, 174) * mm, "end": v(58, 174) * mm});
            skLineSegment(sketch, "E18.0.8.1", {"start": v(50, 159) * mm, "end": v(58, 159) * mm});
            skLineSegment(sketch, "E18.0.8.2", {"start": v(50, 174) * mm, "end": v(50, 159) * mm});
            skLineSegment(sketch, "E18.0.8.3", {"start": v(58, 174) * mm, "end": v(58, 159) * mm});
            skLineSegment(sketch, "E18.0.9.0", {"start": v(50, 156) * mm, "end": v(58, 156) * mm});
            skLineSegment(sketch, "E18.0.9.1", {"start": v(50, 141) * mm, "end": v(58, 141) * mm});
            skLineSegment(sketch, "E18.0.9.2", {"start": v(50, 156) * mm, "end": v(50, 141) * mm});
            skLineSegment(sketch, "E18.0.9.3", {"start": v(58, 156) * mm, "end": v(58, 141) * mm});
            skLineSegment(sketch, "E18.0.10.0", {"start": v(50, 138) * mm, "end": v(58, 138) * mm});
            skLineSegment(sketch, "E18.0.10.1", {"start": v(50, 123) * mm, "end": v(58, 123) * mm});
            skLineSegment(sketch, "E18.0.10.2", {"start": v(50, 138) * mm, "end": v(50, 123) * mm});
            skLineSegment(sketch, "E18.0.10.3", {"start": v(58, 138) * mm, "end": v(58, 123) * mm});
            skLineSegment(sketch, "E18.0.11.0", {"start": v(50, 120) * mm, "end": v(58, 120) * mm});
            skLineSegment(sketch, "E18.0.11.1", {"start": v(50, 105) * mm, "end": v(58, 105) * mm});
            skLineSegment(sketch, "E18.0.11.2", {"start": v(50, 120) * mm, "end": v(50, 105) * mm});
            skLineSegment(sketch, "E18.0.11.3", {"start": v(58, 120) * mm, "end": v(58, 105) * mm});
            skLineSegment(sketch, "E18.0.12.0", {"start": v(50, 102) * mm, "end": v(58, 102) * mm});
            skLineSegment(sketch, "E18.0.12.1", {"start": v(50, 87) * mm, "end": v(58, 87) * mm});
            skLineSegment(sketch, "E18.0.12.2", {"start": v(50, 102) * mm, "end": v(50, 87) * mm});
            skLineSegment(sketch, "E18.0.12.3", {"start": v(58, 102) * mm, "end": v(58, 87) * mm});
            skLineSegment(sketch, "E18.0.13.0", {"start": v(50, 84) * mm, "end": v(58, 84) * mm});
            skLineSegment(sketch, "E18.0.13.1", {"start": v(50, 69) * mm, "end": v(58, 69) * mm});
            skLineSegment(sketch, "E18.0.13.2", {"start": v(50, 84) * mm, "end": v(50, 69) * mm});
            skLineSegment(sketch, "E18.0.13.3", {"start": v(58, 84) * mm, "end": v(58, 69) * mm});
            skLineSegment(sketch, "E18.0.14.0", {"start": v(50, 66) * mm, "end": v(58, 66) * mm});
            skLineSegment(sketch, "E18.0.14.1", {"start": v(50, 51) * mm, "end": v(58, 51) * mm});
            skLineSegment(sketch, "E18.0.14.2", {"start": v(50, 66) * mm, "end": v(50, 51) * mm});
            skLineSegment(sketch, "E18.0.14.3", {"start": v(58, 66) * mm, "end": v(58, 51) * mm});
            skLineSegment(sketch, "E18.0.15.0", {"start": v(50, 48) * mm, "end": v(58, 48) * mm});
            skLineSegment(sketch, "E18.0.15.1", {"start": v(50, 33) * mm, "end": v(58, 33) * mm});
            skLineSegment(sketch, "E18.0.15.2", {"start": v(50, 48) * mm, "end": v(50, 33) * mm});
            skLineSegment(sketch, "E18.0.15.3", {"start": v(58, 48) * mm, "end": v(58, 33) * mm});
            skLineSegment(sketch, "E18.0.16.0", {"start": v(50, 30) * mm, "end": v(58, 30) * mm});
            skLineSegment(sketch, "E18.0.16.1", {"start": v(50, 15) * mm, "end": v(58, 15) * mm});
            skLineSegment(sketch, "E18.0.16.2", {"start": v(50, 30) * mm, "end": v(50, 15) * mm});
            skLineSegment(sketch, "E18.0.16.3", {"start": v(58, 30) * mm, "end": v(58, 15) * mm});
            skLineSegment(sketch, "E18.1.0.0", {"start": v(61, 318) * mm, "end": v(69, 318) * mm});
            skLineSegment(sketch, "E18.1.0.1", {"start": v(61, 303) * mm, "end": v(69, 303) * mm});
            skLineSegment(sketch, "E18.1.0.2", {"start": v(61, 318) * mm, "end": v(61, 303) * mm});
            skLineSegment(sketch, "E18.1.0.3", {"start": v(69, 318) * mm, "end": v(69, 303) * mm});
            skLineSegment(sketch, "E18.1.1.0", {"start": v(61, 300) * mm, "end": v(69, 300) * mm});
            skLineSegment(sketch, "E18.1.1.1", {"start": v(61, 285) * mm, "end": v(69, 285) * mm});
            skLineSegment(sketch, "E18.1.1.2", {"start": v(61, 300) * mm, "end": v(61, 285) * mm});
            skLineSegment(sketch, "E18.1.1.3", {"start": v(69, 300) * mm, "end": v(69, 285) * mm});
            skLineSegment(sketch, "E18.1.2.0", {"start": v(61, 282) * mm, "end": v(69, 282) * mm});
            skLineSegment(sketch, "E18.1.2.1", {"start": v(61, 267) * mm, "end": v(69, 267) * mm});
            skLineSegment(sketch, "E18.1.2.2", {"start": v(61, 282) * mm, "end": v(61, 267) * mm});
            skLineSegment(sketch, "E18.1.2.3", {"start": v(69, 282) * mm, "end": v(69, 267) * mm});
            skLineSegment(sketch, "E18.1.3.0", {"start": v(61, 264) * mm, "end": v(69, 264) * mm});
            skLineSegment(sketch, "E18.1.3.1", {"start": v(61, 249) * mm, "end": v(69, 249) * mm});
            skLineSegment(sketch, "E18.1.3.2", {"start": v(61, 264) * mm, "end": v(61, 249) * mm});
            skLineSegment(sketch, "E18.1.3.3", {"start": v(69, 264) * mm, "end": v(69, 249) * mm});
            skLineSegment(sketch, "E18.1.4.0", {"start": v(61, 246) * mm, "end": v(69, 246) * mm});
            skLineSegment(sketch, "E18.1.4.1", {"start": v(61, 231) * mm, "end": v(69, 231) * mm});
            skLineSegment(sketch, "E18.1.4.2", {"start": v(61, 246) * mm, "end": v(61, 231) * mm});
            skLineSegment(sketch, "E18.1.4.3", {"start": v(69, 246) * mm, "end": v(69, 231) * mm});
            skLineSegment(sketch, "E18.1.5.0", {"start": v(61, 228) * mm, "end": v(69, 228) * mm});
            skLineSegment(sketch, "E18.1.5.1", {"start": v(61, 213) * mm, "end": v(69, 213) * mm});
            skLineSegment(sketch, "E18.1.5.2", {"start": v(61, 228) * mm, "end": v(61, 213) * mm});
            skLineSegment(sketch, "E18.1.5.3", {"start": v(69, 228) * mm, "end": v(69, 213) * mm});
            skLineSegment(sketch, "E18.1.6.0", {"start": v(61, 210) * mm, "end": v(69, 210) * mm});
            skLineSegment(sketch, "E18.1.6.1", {"start": v(61, 195) * mm, "end": v(69, 195) * mm});
            skLineSegment(sketch, "E18.1.6.2", {"start": v(61, 210) * mm, "end": v(61, 195) * mm});
            skLineSegment(sketch, "E18.1.6.3", {"start": v(69, 210) * mm, "end": v(69, 195) * mm});
            skLineSegment(sketch, "E18.1.7.0", {"start": v(61, 192) * mm, "end": v(69, 192) * mm});
            skLineSegment(sketch, "E18.1.7.1", {"start": v(61, 177) * mm, "end": v(69, 177) * mm});
            skLineSegment(sketch, "E18.1.7.2", {"start": v(61, 192) * mm, "end": v(61, 177) * mm});
            skLineSegment(sketch, "E18.1.7.3", {"start": v(69, 192) * mm, "end": v(69, 177) * mm});
            skLineSegment(sketch, "E18.1.8.0", {"start": v(61, 174) * mm, "end": v(69, 174) * mm});
            skLineSegment(sketch, "E18.1.8.1", {"start": v(61, 159) * mm, "end": v(69, 159) * mm});
            skLineSegment(sketch, "E18.1.8.2", {"start": v(61, 174) * mm, "end": v(61, 159) * mm});
            skLineSegment(sketch, "E18.1.8.3", {"start": v(69, 174) * mm, "end": v(69, 159) * mm});
            skLineSegment(sketch, "E18.1.9.0", {"start": v(61, 156) * mm, "end": v(69, 156) * mm});
            skLineSegment(sketch, "E18.1.9.1", {"start": v(61, 141) * mm, "end": v(69, 141) * mm});
            skLineSegment(sketch, "E18.1.9.2", {"start": v(61, 156) * mm, "end": v(61, 141) * mm});
            skLineSegment(sketch, "E18.1.9.3", {"start": v(69, 156) * mm, "end": v(69, 141) * mm});
            skLineSegment(sketch, "E18.1.10.0", {"start": v(61, 138) * mm, "end": v(69, 138) * mm});
            skLineSegment(sketch, "E18.1.10.1", {"start": v(61, 123) * mm, "end": v(69, 123) * mm});
            skLineSegment(sketch, "E18.1.10.2", {"start": v(61, 138) * mm, "end": v(61, 123) * mm});
            skLineSegment(sketch, "E18.1.10.3", {"start": v(69, 138) * mm, "end": v(69, 123) * mm});
            skLineSegment(sketch, "E18.1.11.0", {"start": v(61, 120) * mm, "end": v(69, 120) * mm});
            skLineSegment(sketch, "E18.1.11.1", {"start": v(61, 105) * mm, "end": v(69, 105) * mm});
            skLineSegment(sketch, "E18.1.11.2", {"start": v(61, 120) * mm, "end": v(61, 105) * mm});
            skLineSegment(sketch, "E18.1.11.3", {"start": v(69, 120) * mm, "end": v(69, 105) * mm});
            skLineSegment(sketch, "E18.1.12.0", {"start": v(61, 102) * mm, "end": v(69, 102) * mm});
            skLineSegment(sketch, "E18.1.12.1", {"start": v(61, 87) * mm, "end": v(69, 87) * mm});
            skLineSegment(sketch, "E18.1.12.2", {"start": v(61, 102) * mm, "end": v(61, 87) * mm});
            skLineSegment(sketch, "E18.1.12.3", {"start": v(69, 102) * mm, "end": v(69, 87) * mm});
            skLineSegment(sketch, "E18.1.13.0", {"start": v(61, 84) * mm, "end": v(69, 84) * mm});
            skLineSegment(sketch, "E18.1.13.1", {"start": v(61, 69) * mm, "end": v(69, 69) * mm});
            skLineSegment(sketch, "E18.1.13.2", {"start": v(61, 84) * mm, "end": v(61, 69) * mm});
            skLineSegment(sketch, "E18.1.13.3", {"start": v(69, 84) * mm, "end": v(69, 69) * mm});
            skLineSegment(sketch, "E18.1.14.0", {"start": v(61, 66) * mm, "end": v(69, 66) * mm});
            skLineSegment(sketch, "E18.1.14.1", {"start": v(61, 51) * mm, "end": v(69, 51) * mm});
            skLineSegment(sketch, "E18.1.14.2", {"start": v(61, 66) * mm, "end": v(61, 51) * mm});
            skLineSegment(sketch, "E18.1.14.3", {"start": v(69, 66) * mm, "end": v(69, 51) * mm});
            skLineSegment(sketch, "E18.1.15.0", {"start": v(61, 48) * mm, "end": v(69, 48) * mm});
            skLineSegment(sketch, "E18.1.15.1", {"start": v(61, 33) * mm, "end": v(69, 33) * mm});
            skLineSegment(sketch, "E18.1.15.2", {"start": v(61, 48) * mm, "end": v(61, 33) * mm});
            skLineSegment(sketch, "E18.1.15.3", {"start": v(69, 48) * mm, "end": v(69, 33) * mm});
            skLineSegment(sketch, "E18.1.16.0", {"start": v(61, 30) * mm, "end": v(69, 30) * mm});
            skLineSegment(sketch, "E18.1.16.1", {"start": v(61, 15) * mm, "end": v(69, 15) * mm});
            skLineSegment(sketch, "E18.1.16.2", {"start": v(61, 30) * mm, "end": v(61, 15) * mm});
            skLineSegment(sketch, "E18.1.16.3", {"start": v(69, 30) * mm, "end": v(69, 15) * mm});
            skLineSegment(sketch, "E18.2.0.0", {"start": v(72, 318) * mm, "end": v(80, 318) * mm});
            skLineSegment(sketch, "E18.2.0.1", {"start": v(72, 303) * mm, "end": v(80, 303) * mm});
            skLineSegment(sketch, "E18.2.0.2", {"start": v(72, 318) * mm, "end": v(72, 303) * mm});
            skLineSegment(sketch, "E18.2.0.3", {"start": v(80, 318) * mm, "end": v(80, 303) * mm});
            skLineSegment(sketch, "E18.2.1.0", {"start": v(72, 300) * mm, "end": v(80, 300) * mm});
            skLineSegment(sketch, "E18.2.1.1", {"start": v(72, 285) * mm, "end": v(80, 285) * mm});
            skLineSegment(sketch, "E18.2.1.2", {"start": v(72, 300) * mm, "end": v(72, 285) * mm});
            skLineSegment(sketch, "E18.2.1.3", {"start": v(80, 300) * mm, "end": v(80, 285) * mm});
            skLineSegment(sketch, "E18.2.2.0", {"start": v(72, 282) * mm, "end": v(80, 282) * mm});
            skLineSegment(sketch, "E18.2.2.1", {"start": v(72, 267) * mm, "end": v(80, 267) * mm});
            skLineSegment(sketch, "E18.2.2.2", {"start": v(72, 282) * mm, "end": v(72, 267) * mm});
            skLineSegment(sketch, "E18.2.2.3", {"start": v(80, 282) * mm, "end": v(80, 267) * mm});
            skLineSegment(sketch, "E18.2.3.0", {"start": v(72, 264) * mm, "end": v(80, 264) * mm});
            skLineSegment(sketch, "E18.2.3.1", {"start": v(72, 249) * mm, "end": v(80, 249) * mm});
            skLineSegment(sketch, "E18.2.3.2", {"start": v(72, 264) * mm, "end": v(72, 249) * mm});
            skLineSegment(sketch, "E18.2.3.3", {"start": v(80, 264) * mm, "end": v(80, 249) * mm});
            skLineSegment(sketch, "E18.2.4.0", {"start": v(72, 246) * mm, "end": v(80, 246) * mm});
            skLineSegment(sketch, "E18.2.4.1", {"start": v(72, 231) * mm, "end": v(80, 231) * mm});
            skLineSegment(sketch, "E18.2.4.2", {"start": v(72, 246) * mm, "end": v(72, 231) * mm});
            skLineSegment(sketch, "E18.2.4.3", {"start": v(80, 246) * mm, "end": v(80, 231) * mm});
            skLineSegment(sketch, "E18.2.5.0", {"start": v(72, 228) * mm, "end": v(80, 228) * mm});
            skLineSegment(sketch, "E18.2.5.1", {"start": v(72, 213) * mm, "end": v(80, 213) * mm});
            skLineSegment(sketch, "E18.2.5.2", {"start": v(72, 228) * mm, "end": v(72, 213) * mm});
            skLineSegment(sketch, "E18.2.5.3", {"start": v(80, 228) * mm, "end": v(80, 213) * mm});
            skLineSegment(sketch, "E18.2.6.0", {"start": v(72, 210) * mm, "end": v(80, 210) * mm});
            skLineSegment(sketch, "E18.2.6.1", {"start": v(72, 195) * mm, "end": v(80, 195) * mm});
            skLineSegment(sketch, "E18.2.6.2", {"start": v(72, 210) * mm, "end": v(72, 195) * mm});
            skLineSegment(sketch, "E18.2.6.3", {"start": v(80, 210) * mm, "end": v(80, 195) * mm});
            skLineSegment(sketch, "E18.2.7.0", {"start": v(72, 192) * mm, "end": v(80, 192) * mm});
            skLineSegment(sketch, "E18.2.7.1", {"start": v(72, 177) * mm, "end": v(80, 177) * mm});
            skLineSegment(sketch, "E18.2.7.2", {"start": v(72, 192) * mm, "end": v(72, 177) * mm});
            skLineSegment(sketch, "E18.2.7.3", {"start": v(80, 192) * mm, "end": v(80, 177) * mm});
            skLineSegment(sketch, "E18.2.8.0", {"start": v(72, 174) * mm, "end": v(80, 174) * mm});
            skLineSegment(sketch, "E18.2.8.1", {"start": v(72, 159) * mm, "end": v(80, 159) * mm});
            skLineSegment(sketch, "E18.2.8.2", {"start": v(72, 174) * mm, "end": v(72, 159) * mm});
            skLineSegment(sketch, "E18.2.8.3", {"start": v(80, 174) * mm, "end": v(80, 159) * mm});
            skLineSegment(sketch, "E18.2.9.0", {"start": v(72, 156) * mm, "end": v(80, 156) * mm});
            skLineSegment(sketch, "E18.2.9.1", {"start": v(72, 141) * mm, "end": v(80, 141) * mm});
            skLineSegment(sketch, "E18.2.9.2", {"start": v(72, 156) * mm, "end": v(72, 141) * mm});
            skLineSegment(sketch, "E18.2.9.3", {"start": v(80, 156) * mm, "end": v(80, 141) * mm});
            skLineSegment(sketch, "E18.2.10.0", {"start": v(72, 138) * mm, "end": v(80, 138) * mm});
            skLineSegment(sketch, "E18.2.10.1", {"start": v(72, 123) * mm, "end": v(80, 123) * mm});
            skLineSegment(sketch, "E18.2.10.2", {"start": v(72, 138) * mm, "end": v(72, 123) * mm});
            skLineSegment(sketch, "E18.2.10.3", {"start": v(80, 138) * mm, "end": v(80, 123) * mm});
            skLineSegment(sketch, "E18.2.11.0", {"start": v(72, 120) * mm, "end": v(80, 120) * mm});
            skLineSegment(sketch, "E18.2.11.1", {"start": v(72, 105) * mm, "end": v(80, 105) * mm});
            skLineSegment(sketch, "E18.2.11.2", {"start": v(72, 120) * mm, "end": v(72, 105) * mm});
            skLineSegment(sketch, "E18.2.11.3", {"start": v(80, 120) * mm, "end": v(80, 105) * mm});
            skLineSegment(sketch, "E18.2.12.0", {"start": v(72, 102) * mm, "end": v(80, 102) * mm});
            skLineSegment(sketch, "E18.2.12.1", {"start": v(72, 87) * mm, "end": v(80, 87) * mm});
            skLineSegment(sketch, "E18.2.12.2", {"start": v(72, 102) * mm, "end": v(72, 87) * mm});
            skLineSegment(sketch, "E18.2.12.3", {"start": v(80, 102) * mm, "end": v(80, 87) * mm});
            skLineSegment(sketch, "E18.2.13.0", {"start": v(72, 84) * mm, "end": v(80, 84) * mm});
            skLineSegment(sketch, "E18.2.13.1", {"start": v(72, 69) * mm, "end": v(80, 69) * mm});
            skLineSegment(sketch, "E18.2.13.2", {"start": v(72, 84) * mm, "end": v(72, 69) * mm});
            skLineSegment(sketch, "E18.2.13.3", {"start": v(80, 84) * mm, "end": v(80, 69) * mm});
            skLineSegment(sketch, "E18.2.14.0", {"start": v(72, 66) * mm, "end": v(80, 66) * mm});
            skLineSegment(sketch, "E18.2.14.1", {"start": v(72, 51) * mm, "end": v(80, 51) * mm});
            skLineSegment(sketch, "E18.2.14.2", {"start": v(72, 66) * mm, "end": v(72, 51) * mm});
            skLineSegment(sketch, "E18.2.14.3", {"start": v(80, 66) * mm, "end": v(80, 51) * mm});
            skLineSegment(sketch, "E18.2.15.0", {"start": v(72, 48) * mm, "end": v(80, 48) * mm});
            skLineSegment(sketch, "E18.2.15.1", {"start": v(72, 33) * mm, "end": v(80, 33) * mm});
            skLineSegment(sketch, "E18.2.15.2", {"start": v(72, 48) * mm, "end": v(72, 33) * mm});
            skLineSegment(sketch, "E18.2.15.3", {"start": v(80, 48) * mm, "end": v(80, 33) * mm});
            skLineSegment(sketch, "E18.2.16.0", {"start": v(72, 30) * mm, "end": v(80, 30) * mm});
            skLineSegment(sketch, "E18.2.16.1", {"start": v(72, 15) * mm, "end": v(80, 15) * mm});
            skLineSegment(sketch, "E18.2.16.2", {"start": v(72, 30) * mm, "end": v(72, 15) * mm});
            skLineSegment(sketch, "E18.2.16.3", {"start": v(80, 30) * mm, "end": v(80, 15) * mm});
            skLineSegment(sketch, "E18.direction1", {"start": v(50, 318) * mm, "end": v(61, 318) * mm, "construction": true});
            skLineSegment(sketch, "E18.direction2", {"start": v(50, 318) * mm, "end": v(50, 300) * mm, "construction": true});
            skSolve(sketch);
        }
        {
            var Q0;
            Q0 = qSketchRegion(id + "F21", true);
            extrude(context, id + "F22", {"entities" : qUnion([Q0]), "operationType" : NewBodyOperationType.REMOVE, "oppositeDirection" : true, "depth" : 3 * mm});
        }
        {
            var Q0;
            Q0=makeQuery(id+"F11.opLoft","SWEPT_FACE",FACE,{"disambiguationData":[OSD([sQuery(id+"F8.wireOp",EDGE,"E7.top"),sQuery(id+"F8.wireOp",EDGE,"E7.left"),sQuery(id+"F8.wireOp",EDGE,"E7.right"),sQuery(id+"F10.wireOp",EDGE,"E8.top"),sQuery(id+"F10.wireOp",EDGE,"E8.left"),sQuery(id+"F10.wireOp",EDGE,"E8.right")])]});
            var sketch = newSketch(context, id + "F23", { "sketchPlane" : qUnion([Q0])});
            skLineSegment(sketch, "E19", {"start": v(100, 316.94) * mm, "end": v(145.4, 316.94) * mm});
            skPoint(sketch, "E20", {"position": v(147.5, 338.06) * mm});
            skLineSegment(sketch, "E21", {"start": v(100, 340.94) * mm, "end": v(147.79, 340.94) * mm});
            skLineSegment(sketch, "E22", {"start": v(147.79, 340.94) * mm, "end": v(145.4, 316.94) * mm});
            skLineSegment(sketch, "E23", {"start": v(30, 316.94) * mm, "end": v(-15.4, 316.94) * mm});
            skLineSegment(sketch, "E24", {"start": v(30, 340.94) * mm, "end": v(-17.79, 340.94) * mm});
            skLineSegment(sketch, "E25", {"start": v(-17.79, 340.94) * mm, "end": v(-15.4, 316.94) * mm});
            skLineSegment(sketch, "E26", {"start": v(30, 316.94) * mm, "end": v(30, 340.94) * mm});
            skLineSegment(sketch, "E27", {"start": v(100, 316.94) * mm, "end": v(100, 340.94) * mm});
            skSolve(sketch);
        }
        {
            var Q0;
            Q0 = qSketchRegion(id + "F23", true);
            extrude(context, id + "F24", {"entities" : qUnion([Q0]), "operationType" : NewBodyOperationType.REMOVE, "oppositeDirection" : true, "depth" : 3 * mm});
        }
        {
            var Q0;
            Q0=makeQuery(id+"F11.opLoft","SWEPT_FACE",FACE,{"disambiguationData":[OSD([sQuery(id+"F8.wireOp",EDGE,"E7.bottom"),sQuery(id+"F8.wireOp",EDGE,"E7.top"),sQuery(id+"F8.wireOp",EDGE,"E7.right"),sQuery(id+"F10.wireOp",EDGE,"E8.bottom"),sQuery(id+"F10.wireOp",EDGE,"E8.top"),sQuery(id+"F10.wireOp",EDGE,"E8.right")])]});
            var sketch = newSketch(context, id + "F25", { "sketchPlane" : qUnion([Q0])});
            skLineSegment(sketch, "E28", {"start": v(-147.79, 340.94) * mm, "end": v(17.79, 340.94) * mm});
            skLineSegment(sketch, "E29", {"start": v(-147.79, 340.94) * mm, "end": v(-145.4, 316.94) * mm});
            skLineSegment(sketch, "E30", {"start": v(-145.4, 316.94) * mm, "end": v(15.4, 316.94) * mm});
            skLineSegment(sketch, "E31", {"start": v(15.4, 316.94) * mm, "end": v(17.79, 340.94) * mm});
            skSolve(sketch);
        }
        {
            var Q0;
            Q0 = qSketchRegion(id + "F25", true);
            extrude(context, id + "F26", {"entities" : qUnion([Q0]), "operationType" : NewBodyOperationType.REMOVE, "oppositeDirection" : true, "depth" : 3 * mm});
        }
        {
            var Q0;
            Q0=makeQuery(id+"F11.opLoft","SWEPT_FACE",FACE,{"disambiguationData":[OSD([sQuery(id+"F8.wireOp",EDGE,"E7.bottom"),sQuery(id+"F8.wireOp",EDGE,"E7.left"),sQuery(id+"F8.wireOp",EDGE,"E7.right"),sQuery(id+"F10.wireOp",EDGE,"E8.bottom"),sQuery(id+"F10.wireOp",EDGE,"E8.left"),sQuery(id+"F10.wireOp",EDGE,"E8.right")])]});
            var sketch = newSketch(context, id + "F27", { "sketchPlane" : qUnion([Q0])});
            skLineSegment(sketch, "E32", {"start": v(-147.79, 328) * mm, "end": v(17.79, 328) * mm});
            skLineSegment(sketch, "E33", {"start": v(-147.79, 328) * mm, "end": v(-145.4, 304) * mm});
            skLineSegment(sketch, "E34", {"start": v(-145.4, 304) * mm, "end": v(15.4, 304) * mm});
            skLineSegment(sketch, "E35", {"start": v(15.4, 304) * mm, "end": v(17.79, 328) * mm});
            skSolve(sketch);
        }
        {
            var Q0;
            Q0 = qSketchRegion(id + "F27", true);
            extrude(context, id + "F28", {"entities" : qUnion([Q0]), "operationType" : NewBodyOperationType.REMOVE, "oppositeDirection" : true, "depth" : 3 * mm});
        }
        {
            var Q0;
            Q0=makeQuery(id+"F11.opLoft","SWEPT_FACE",FACE,{"disambiguationData":[OSD([sQuery(id+"F8.wireOp",EDGE,"E7.bottom"),sQuery(id+"F8.wireOp",EDGE,"E7.top"),sQuery(id+"F8.wireOp",EDGE,"E7.left"),sQuery(id+"F10.wireOp",EDGE,"E8.bottom"),sQuery(id+"F10.wireOp",EDGE,"E8.top"),sQuery(id+"F10.wireOp",EDGE,"E8.left")])]});
            var sketch = newSketch(context, id + "F29", { "sketchPlane" : qUnion([Q0])});
            skLineSegment(sketch, "E36", {"start": v(-17.79, 328) * mm, "end": v(147.79, 328) * mm});
            skLineSegment(sketch, "E37", {"start": v(147.79, 328) * mm, "end": v(145.4, 304) * mm});
            skLineSegment(sketch, "E38", {"start": v(145.4, 304) * mm, "end": v(-15.4, 304) * mm});
            skLineSegment(sketch, "E39", {"start": v(-15.4, 304) * mm, "end": v(-17.79, 328) * mm});
            skSolve(sketch);
        }
        {
            var Q0;
            Q0 = qSketchRegion(id + "F29", true);
            extrude(context, id + "F30", {"entities" : qUnion([Q0]), "operationType" : NewBodyOperationType.REMOVE, "oppositeDirection" : true, "depth" : 3 * mm});
        }
        {
            var Q0;
            Q0=qCreatedBy(makeId("Top.planeOp"),FACE);
            var sketch = newSketch(context, id + "F31", { "sketchPlane" : qUnion([Q0])});
            skLineSegment(sketch, "E40.bottom", {"start": v(87.5, 0) * mm, "end": v(42.5, 0) * mm});
            skLineSegment(sketch, "E40.top", {"start": v(87.5, 25) * mm, "end": v(42.5, 25) * mm});
            skLineSegment(sketch, "E40.left", {"start": v(87.5, 0) * mm, "end": v(87.5, 25) * mm});
            skLineSegment(sketch, "E40.right", {"start": v(42.5, 0) * mm, "end": v(42.5, 25) * mm});
            skSolve(sketch);
        }
        {
            var Q0;
            Q0=makeQuery(id+"F31.imprint","IMPRINT",FACE,{"disambiguationData":[TD([[makeQuery(id+"F31.imprint","IMPRINT",EDGE,{"derivedFrom":sQuery(id+"F31.wireOp",EDGE,"E40.bottom")}),-1.0]])]});
            extrude(context, id + "F32", {"entities" : qUnion([Q0]), "operationType" : NewBodyOperationType.REMOVE, "depth" : 340 * mm});
        }
    });
